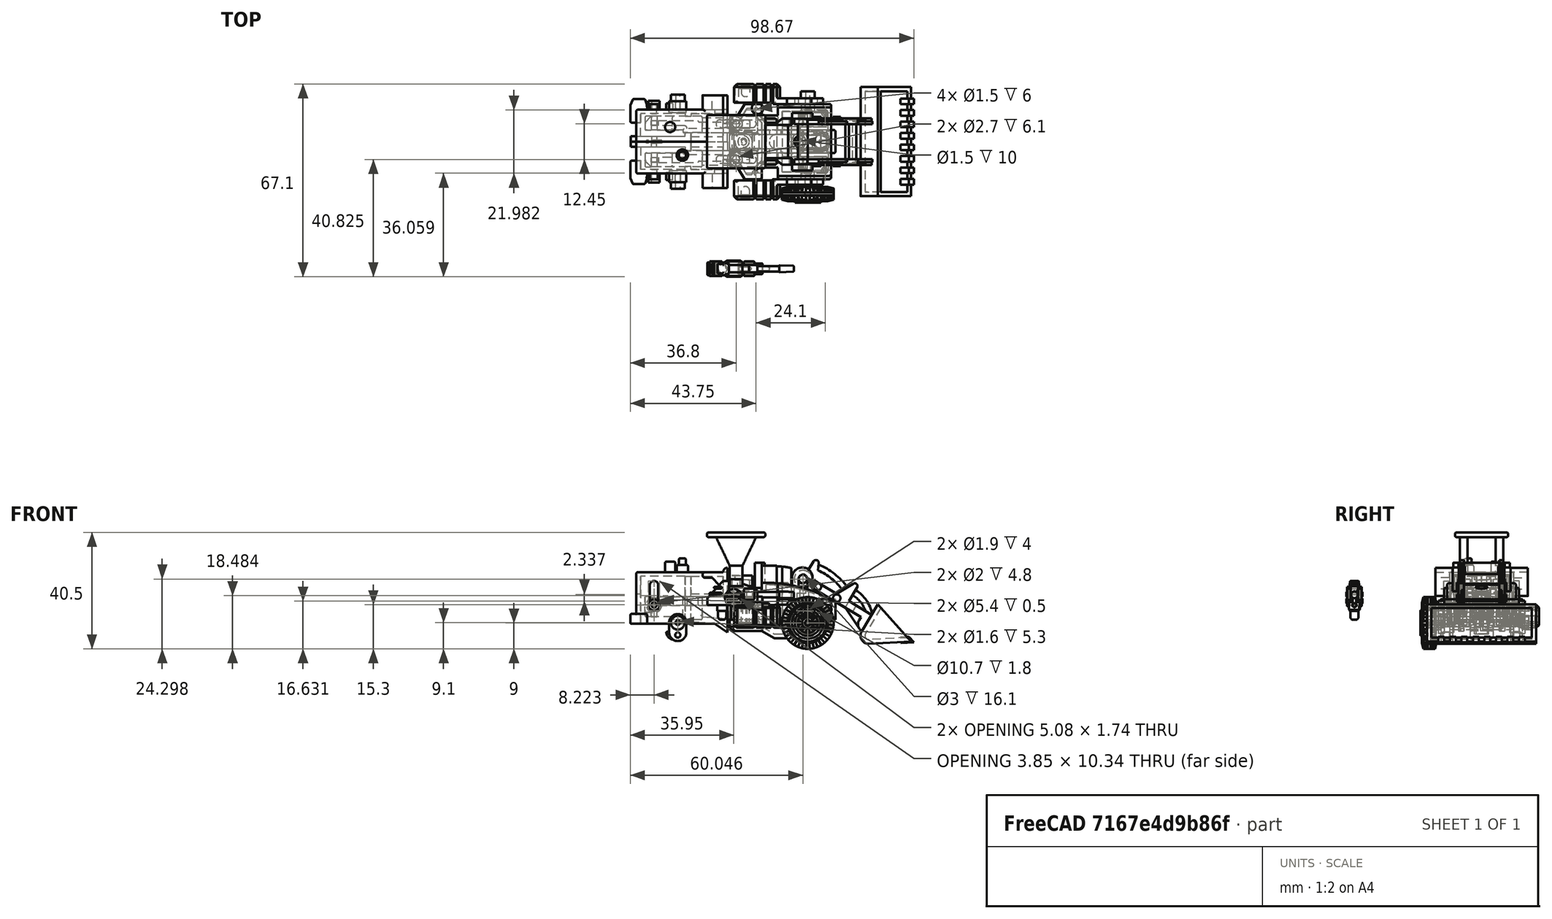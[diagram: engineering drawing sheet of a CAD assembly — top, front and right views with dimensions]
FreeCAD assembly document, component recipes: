
FREECAD ASSEMBLY — COMPONENT RECIPES ("Scrapper")

This assembly document has 14 components, labeled P0..P13 below (a component is one placed body or linked part). 14 of them carry a construction recipe — the FreeCAD feature program that regenerates the part from scratch, quoted from this document or its linked companion documents; the rest are supplied as boundary geometry only. No exploded tour is included for this assembly.
NOTE — this tour is split across 4 documents so each fits a 32k-token context. This is document 1: the component sections continue in the remaining 3 documents, each repeating the header above.
COMPONENT P0 — recipe-attached ("Rear_Torso", modeled in this document).
Construction recipe (the document's own serialized feature program — sketch geometry with constraints, then the solid features built on it; lengths are millimeters unless a unit is written):

FEATURE [Sketcher::SketchObject] Sketch
  ArcFitTolerance = 1e-06
  AttachmentSupport = -> [XY_Plane]
  FullyConstrained = true
  MakeInternals = false
  MapMode = 5
  sketch-geometry (50):
    g0: LineSegment StartX=0 StartY=13.05 StartZ=0 EndX=0 EndY=-13.05 EndZ=0
    g1: LineSegment StartX=0 StartY=-13.05 StartZ=0 EndX=-18.5 EndY=-13.05 EndZ=0
    g2: LineSegment StartX=0 StartY=13.05 StartZ=0 EndX=-18.5 EndY=13.05 EndZ=0
    g3: LineSegment StartX=-17 StartY=10.55 StartZ=0 EndX=-3.5 EndY=10.55 EndZ=0
    g4: LineSegment StartX=-1.5 StartY=5.2 StartZ=0 EndX=-10.8 EndY=5.2 EndZ=0
    g5: LineSegment StartX=-10.8 StartY=5.2 StartZ=0 EndX=-10.8 EndY=3 EndZ=0
    g6: LineSegment StartX=-10.8 StartY=3 StartZ=0 EndX=-1.5 EndY=3 EndZ=0
    g7: LineSegment StartX=-1.5 StartY=3 StartZ=0 EndX=-1.5 EndY=-3 EndZ=0
    g8: LineSegment StartX=-1.5 StartY=-3 StartZ=0 EndX=-10.8 EndY=-3 EndZ=0
    g9: LineSegment StartX=-10.8 StartY=-3 StartZ=0 EndX=-10.8 EndY=-5.2 EndZ=0
    g10: LineSegment StartX=-10.8 StartY=-5.2 StartZ=0 EndX=-1.5 EndY=-5.2 EndZ=0
    g11: LineSegment StartX=-3.5 StartY=-10.55 StartZ=0 EndX=-17 EndY=-10.55 EndZ=0
    g12: ArcOfCircle CenterX=-1.5 CenterY=10.55 CenterZ=0 NormalX=0 NormalY=0 NormalZ=1 AngleXU=0 Radius=2 StartAngle=3.14159 EndAngle=4.71239
    g13: LineSegment StartX=-1.5 StartY=8.55 StartZ=0 EndX=-1.5 EndY=5.2 EndZ=0
    g14: ArcOfCircle CenterX=-1.5 CenterY=-10.55 CenterZ=0 NormalX=0 NormalY=0 NormalZ=1 AngleXU=0 Radius=2 StartAngle=1.5708 EndAngle=3.14159
    g15: LineSegment StartX=-1.5 StartY=-5.2 StartZ=0 EndX=-1.5 EndY=-8.55 EndZ=0
    g16: LineSegment StartX=-18.5 StartY=-13.05 StartZ=0 EndX=-18.5 EndY=-9.05 EndZ=0
    g17: LineSegment StartX=-18.5 StartY=-9.05 StartZ=0 EndX=-24.1 EndY=-9.05 EndZ=0
    g18: LineSegment StartX=-24.1 StartY=-9.05 StartZ=0 EndX=-24.1 EndY=-13.05 EndZ=0
    g19: LineSegment StartX=-24.1 StartY=-13.05 StartZ=0 EndX=-30.1 EndY=-13.05 EndZ=0
    g20: LineSegment StartX=-30.1 StartY=-13.05 StartZ=0 EndX=-32.6 EndY=-8.9 EndZ=0
    g21: LineSegment StartX=-32.6 StartY=-8.9 StartZ=0 EndX=-35.3 EndY=-8.9 EndZ=0
    g22: LineSegment StartX=-35.3 StartY=-8.9 StartZ=0 EndX=-35.3 EndY=8.9 EndZ=0
    g23: LineSegment StartX=-35.3 StartY=8.9 StartZ=0 EndX=-32.6 EndY=8.9 EndZ=0
    g24: LineSegment StartX=-32.6 StartY=8.9 StartZ=0 EndX=-30.1 EndY=13.05 EndZ=0
    g25: LineSegment StartX=-30.1 StartY=13.05 StartZ=0 EndX=-24.1 EndY=13.05 EndZ=0
    g26: LineSegment StartX=-24.1 StartY=13.05 StartZ=0 EndX=-24.1 EndY=9.05 EndZ=0
    g27: LineSegment StartX=-24.1 StartY=9.05 StartZ=0 EndX=-18.5 EndY=9.05 EndZ=0
    g28: LineSegment StartX=-18.5 StartY=9.05 StartZ=0 EndX=-18.5 EndY=13.05 EndZ=0
    g29: LineSegment StartX=-17 StartY=-10.55 StartZ=0 EndX=-17 EndY=-8.55 EndZ=0
    g30: ArcOfCircle CenterX=-18 CenterY=-8.55 CenterZ=0 NormalX=0 NormalY=0 NormalZ=1 AngleXU=0 Radius=1 StartAngle=5e-16 EndAngle=1.5708
    g31: LineSegment StartX=-18 StartY=-7.55 StartZ=0 EndX=-24.6 EndY=-7.55 EndZ=0
    g32: ArcOfCircle CenterX=-24.6 CenterY=-8.55 CenterZ=0 NormalX=0 NormalY=0 NormalZ=1 AngleXU=0 Radius=1 StartAngle=1.5708 EndAngle=3.14159
    g33: LineSegment StartX=-25.6 StartY=-8.55 StartZ=0 EndX=-25.6 EndY=-9.55 EndZ=0
    g34: ArcOfCircle CenterX=-25.6 CenterY=-11.55 CenterZ=0 NormalX=0 NormalY=0 NormalZ=1 AngleXU=0 Radius=2 StartAngle=1.5708 EndAngle=3.14159
    g35: LineSegment StartX=-27.6 StartY=-11.55 StartZ=0 EndX=-29.27 EndY=-11.55 EndZ=0
    g36: LineSegment StartX=-29.27 StartY=-11.55 StartZ=0 EndX=-31.4373 EndY=-7.95236 EndZ=0
    g37: ArcOfCircle CenterX=-32.6 CenterY=-8.9 CenterZ=0 NormalX=0 NormalY=0 NormalZ=1 AngleXU=0 Radius=1.5 StartAngle=0.683822 EndAngle=1.5708
    g38: LineSegment StartX=-32.6 StartY=-7.4 StartZ=0 EndX=-33.8 EndY=-7.4 EndZ=0
    g39: LineSegment StartX=-33.8 StartY=-7.4 StartZ=0 EndX=-33.8 EndY=7.4 EndZ=0
    g40: LineSegment StartX=-33.8 StartY=7.4 StartZ=0 EndX=-32.6 EndY=7.4 EndZ=0
    g41: ArcOfCircle CenterX=-32.6 CenterY=8.9 CenterZ=0 NormalX=0 NormalY=0 NormalZ=1 AngleXU=0 Radius=1.5 StartAngle=4.71239 EndAngle=5.59936
    g42: LineSegment StartX=-31.4373 StartY=7.95236 StartZ=0 EndX=-29.27 EndY=11.55 EndZ=0
    g43: LineSegment StartX=-29.27 StartY=11.55 StartZ=0 EndX=-27.6 EndY=11.55 EndZ=0
    g44: ArcOfCircle CenterX=-25.6 CenterY=11.55 CenterZ=0 NormalX=0 NormalY=0 NormalZ=1 AngleXU=0 Radius=2 StartAngle=3.14159 EndAngle=4.71239
    g45: LineSegment StartX=-25.6 StartY=9.55 StartZ=0 EndX=-25.6 EndY=8.55 EndZ=0
    g46: ArcOfCircle CenterX=-24.6 CenterY=8.55 CenterZ=0 NormalX=0 NormalY=0 NormalZ=1 AngleXU=0 Radius=1 StartAngle=3.14159 EndAngle=4.71239
    g47: LineSegment StartX=-24.6 StartY=7.55 StartZ=0 EndX=-18 EndY=7.55 EndZ=0
    g48: ArcOfCircle CenterX=-18 CenterY=8.55 CenterZ=0 NormalX=0 NormalY=0 NormalZ=1 AngleXU=0 Radius=1 StartAngle=4.71239 EndAngle=6.28319
    g49: LineSegment StartX=-17 StartY=8.55 StartZ=0 EndX=-17 EndY=10.55 EndZ=0
  constraints (158):
    c: Vertical(g0)
    c: Coincident(g1,g0)
    c: Horizontal(g1)
    c: Coincident(g2,g0)
    c: Horizontal(g2)
    c: DistanceY(g0,g0) = 26.1
    c: DistanceY(g-1,g0) = 13.05
    c: PointOnObject(g-1,g0)
    c: DistanceX(g2,g2) = 18.5
    c: DistanceX(g1,g1) = 18.5
    c: Horizontal(g3)
    c: Horizontal(g4)
    c: Coincident(g5,g4)
    c: Vertical(g5)
    c: Coincident(g6,g5)
    c: Horizontal(g6)
    c: Coincident(g7,g6)
    c: Vertical(g7)
    c: Coincident(g8,g7)
    c: Horizontal(g8)
    c: Coincident(g9,g8)
    c: Vertical(g9)
    c: Coincident(g10,g9)
    c: Horizontal(g10)
    c: Horizontal(g11)
    c: DistanceY(g5,g5) = 2.2
    c: DistanceY(g9,g9) = 2.2
    c: DistanceY(g3,g0) = 2.5
    c: DistanceY(g0,g11) = 2.5
    c: Coincident(g12,g3)
    c: Coincident(g13,g12)
    c: Coincident(g13,g4)
    c: Vertical(g13)
    c: Coincident(g14,g11)
    c: Coincident(g15,g10)
    c: Coincident(g15,g14)
    c: Vertical(g15)
    c: DistanceX(g14,g0) = 1.5
    c: DistanceX(g7,g-1) = 1.5
    c: DistanceX(g12,g0) = 1.5
    c: DistanceY(g12,g3) = 0
    c: DistanceY(g11,g14) = 0
    c: DistanceX(g14,g14) = 0
    c: Radius(g12) = 2
    c: Radius(g14) = 2
    c: DistanceY(g7,g7) = 6
    c: DistanceY(g7,g-1) = 3
    c: DistanceX(g12,g12) = 0
    c: DistanceX(g6,g6) = 9.3
    c: DistanceX(g8,g8) = 9.3
    c: Coincident(g16,g1)
    c: Vertical(g16)
    c: Coincident(g17,g16)
    c: Horizontal(g17)
    c: Coincident(g18,g17)
    c: Vertical(g18)
    c: Coincident(g19,g18)
    c: Horizontal(g19)
    c: Coincident(g20,g19)
    c: Coincident(g21,g20)
    c: Horizontal(g21)
    c: Coincident(g22,g21)
    c: Vertical(g22)
    c: Coincident(g23,g22)
    c: Horizontal(g23)
    c: Coincident(g24,g23)
    c: Coincident(g25,g24)
    c: Horizontal(g25)
    c: Coincident(g26,g25)
    c: Vertical(g26)
    c: Coincident(g27,g26)
    c: Horizontal(g27)
    c: Coincident(g28,g27)
    c: Coincident(g28,g2)
    c: Vertical(g28)
    c: DistanceX(g27,g27) = 5.6
    c: DistanceX(g17,g17) = 5.6
    c: DistanceY(g16,g16) = 4
    c: DistanceY(g18,g18) = 4
    c: DistanceY(g28,g28) = 4
    c: DistanceY(g26,g26) = 4
    c: DistanceX(g25,g25) = 6
    c: DistanceX(g19,g19) = 6
    c: DistanceX(g22,g-1) = 35.3
    c: DistanceX(g23,g23) = 2.7
    c: DistanceX(g21,g21) = 2.7
    c: DistanceY(g22,g22) = 17.8
    c: DistanceY(g-1,g22) = 8.9
    c: Coincident(g29,g11)
    c: Vertical(g29)
    c: Coincident(g30,g29)
    c: Coincident(g31,g30)
    c: Horizontal(g31)
    c: Coincident(g32,g31)
    c: Coincident(g33,g32)
    c: Vertical(g33)
    c: Coincident(g34,g33)
    c: Coincident(g35,g34)
    c: Horizontal(g35)
    c: Coincident(g36,g35)
    c: Coincident(g37,g36)
    c: Coincident(g38,g37)
    c: Horizontal(g38)
    c: Coincident(g39,g38)
    c: Vertical(g39)
    c: Coincident(g40,g39)
    c: Horizontal(g40)
    c: Coincident(g41,g40)
    c: Coincident(g42,g41)
    c: Coincident(g43,g42)
    c: Horizontal(g43)
    c: Coincident(g44,g43)
    c: Coincident(g45,g44)
    c: Vertical(g45)
    c: Coincident(g46,g45)
    c: Coincident(g47,g46)
    c: Horizontal(g47)
    c: Coincident(g48,g47)
    c: Coincident(g49,g48)
    c: Coincident(g49,g3)
    c: Vertical(g49)
    c: DistanceX(g22,g39) = 1.5
    c: DistanceY(g46,g26) = 1.5
    c: DistanceY(g17,g31) = 1.5
    c: DistanceX(g16,g29) = 1.5
    c: DistanceX(g32,g17) = 1.5
    c: DistanceX(g45,g26) = 1.5
    c: DistanceX(g27,g48) = 1.5
    c: DistanceY(g48,g48) = 0
    c: DistanceY(g29,g30) = 0
    c: DistanceX(g30,g30) = 0
    c: DistanceX(g32,g31) = 0
    c: DistanceX(g48,g47) = 0
    c: DistanceX(g46,g46) = 0
    c: DistanceY(g46,g45) = 0
    c: Radius(g48) = 1
    c: Radius(g46) = 1
    c: Radius(g30) = 1
    c: Radius(g32) = 1
    c: DistanceY(g32,g32) = 0
    c: Parallel(g20,g36)
    c: Parallel(g42,g24)
    c: DistanceX(g40,g41) = 0
    c: DistanceX(g37,g37) = 0
    c: DistanceY(g20,g38) = 1.5
    c: DistanceY(g39,g23) = 1.5
    c: DistanceX(g34,g33) = 0
    c: DistanceX(g44,g44) = 0
    c: DistanceY(g43,g44) = 0
    c: DistanceY(g34,g34) = 0
    c: Radius(g34) = 2
    c: Radius(g44) = 2
    c: DistanceY(g19,g35) = 1.5
    c: DistanceY(g42,g24) = 1.5
    c: Coincident(g41,g23)
    c: Coincident(g37,g20)
    c: Distance(g36) = 4.2
    c: Distance(g42) = 4.2
FEATURE [PartDesign::Pad] Pad
  Direction = (0,0,1)
  Length = 2
  Length2 = 10
  Profile = -> Sketch
  ReferenceAxis = -> Sketch [N_Axis]
  Refine = true
  Suppressed = false
  Type = 0
FEATURE [Sketcher::SketchObject] Sketch001
  ArcFitTolerance = 1e-06
  AttachmentSupport = -> [Pad]
  ExternalGeometry = -> [Pad]
  FullyConstrained = true
  MakeInternals = false
  MapMode = 5
  Placement = pos=(0,-13.05,0) rot=(1,0,0;1.5708rad)
  sketch-geometry (3):
    g0: LineSegment StartX=-18.5 StartY=2 StartZ=0 EndX=-18.5 EndY=7.6 EndZ=0
    g1: ArcOfCircle CenterX=-22.8718 CenterY=-40.2005 CenterZ=0 NormalX=0 NormalY=0 NormalZ=1 AngleXU=0 Radius=48 StartAngle=1.07413 EndAngle=1.47959
    g2: LineSegment StartX=-18.5 StartY=2 StartZ=0 EndX=0 EndY=2 EndZ=0
  constraints (8):
    c: Coincident(g0,g-3)
    c: Vertical(g0)
    c: Coincident(g1,g0)
    c: Coincident(g1,g-3)
    c: Coincident(g2,g0)
    c: Coincident(g2,g-3)
    c: DistanceY(g0,g0) = 5.6
    c: Radius(g1) = 48
FEATURE [PartDesign::Pad] Pad001
  BaseFeature = -> Pad
  Direction = (0,-1,2e-16)
  Length = 25
  Length2 = 10
  Profile = -> Sketch001
  ReferenceAxis = -> Sketch001 [N_Axis]
  Refine = true
  Reversed = true
  Suppressed = false
  Type = 0
FEATURE [Sketcher::SketchObject] Sketch002
  ArcFitTolerance = 1e-06
  AttachmentSupport = -> [Pad001]
  ExternalGeometry = -> [Pad001]
  FullyConstrained = true
  MakeInternals = false
  MapMode = 5
  Placement = pos=(0,-13.05,3.7e-15) rot=(1,0,0;1.5708rad)
  sketch-geometry (3):
    g0: LineSegment StartX=-17 StartY=2 StartZ=0 EndX=-1.5 EndY=2 EndZ=0
    g1: LineSegment StartX=-17 StartY=2 StartZ=0 EndX=-17 EndY=6.7373 EndZ=0
    g2: ArcOfCircle CenterX=-22.8718 CenterY=-40.2005 CenterZ=0 NormalX=0 NormalY=0 NormalZ=1 AngleXU=0 Radius=47.3036 StartAngle=1.10201 EndAngle=1.44635
  constraints (9):
    c: Horizontal(g0)
    c: Coincident(g1,g0)
    c: Vertical(g1)
    c: Coincident(g2,g1)
    c: Coincident(g2,g0)
    c: Coincident(g2,g-3)
    c: DistanceY(g-4,g0) = 2
    c: DistanceX(g-4,g0) = 1.5
    c: DistanceX(g0,g-5) = 1.5
FEATURE [PartDesign::Pocket] Pocket
  BaseFeature = -> Pad001
  Direction = (0,1,-2e-16)
  Length = 23.6
  Length2 = 5
  Profile = -> Sketch002
  ReferenceAxis = -> Sketch002 [N_Axis]
  Refine = true
  Suppressed = false
  Type = 0
FEATURE [Sketcher::SketchObject] Sketch003
  ArcFitTolerance = 1e-06
  AttachmentSupport = -> [Pocket]
  ExternalGeometry = -> [Pocket]
  FullyConstrained = true
  MakeInternals = false
  MapMode = 5
  Placement = pos=(0,-13.05,3.7e-15) rot=(1,0,0;1.5708rad)
  sketch-geometry (3):
    g0: LineSegment StartX=0 StartY=2 StartZ=0 EndX=-18.5 EndY=2 EndZ=0
    g1: LineSegment StartX=-18.5 StartY=2 StartZ=0 EndX=-18.5 EndY=7.6 EndZ=0
    g2: ArcOfCircle CenterX=-22.8718 CenterY=-40.2005 CenterZ=0 NormalX=0 NormalY=0 NormalZ=1 AngleXU=0 Radius=48 StartAngle=1.07413 EndAngle=1.47959
  constraints (8):
    c: Coincident(g0,g-4)
    c: PointOnObject(g0,g-5)
    c: Horizontal(g0)
    c: Coincident(g1,g0)
    c: Coincident(g1,g-5)
    c: Coincident(g2,g1)
    c: Coincident(g2,g0)
    c: Tangent(g2,g-4)
FEATURE [PartDesign::Pocket] Pocket001
  BaseFeature = -> Pocket
  Direction = (0,1,-2e-16)
  Length = 1.1
  Length2 = 5
  Profile = -> Sketch003
  ReferenceAxis = -> Sketch003 [N_Axis]
  Refine = true
  Suppressed = false
  Type = 0
FEATURE [Sketcher::SketchObject] Sketch004
  ArcFitTolerance = 1e-06
  AttachmentSupport = -> [Pocket001]
  ExternalGeometry = -> [Pocket001]
  FullyConstrained = true
  MakeInternals = false
  MapMode = 5
  Placement = pos=(0,-11.95,4.5e-15) rot=(1,0,0;1.5708rad)
  sketch-geometry (3):
    g0: LineSegment StartX=-17 StartY=6.7373 StartZ=0 EndX=-17 EndY=2 EndZ=0
    g1: LineSegment StartX=-17 StartY=2 StartZ=0 EndX=-1.5 EndY=2 EndZ=0
    g2: ArcOfCircle CenterX=-22.8718 CenterY=-40.2005 CenterZ=0 NormalX=0 NormalY=0 NormalZ=1 AngleXU=0 Radius=47.3036 StartAngle=1.10201 EndAngle=1.44635
  constraints (7):
    c: Coincident(g0,g-4)
    c: Coincident(g0,g-4)
    c: Coincident(g1,g0)
    c: Coincident(g1,g-3)
    c: Coincident(g2,g0)
    c: Coincident(g2,g1)
    c: Tangent(g2,g-3)
FEATURE [PartDesign::Pad] Pad002
  BaseFeature = -> Pocket001
  Direction = (0,-1,2e-16)
  Length = 1.4
  Length2 = 10
  Profile = -> Sketch004
  ReferenceAxis = -> Sketch004 [N_Axis]
  Refine = true
  Reversed = true
  Suppressed = false
  Type = 0
FEATURE [Sketcher::SketchObject] Sketch005
  ArcFitTolerance = 1e-06
  AttachmentSupport = -> [Pad002]
  ExternalGeometry = -> [Pad002]
  FullyConstrained = true
  MakeInternals = false
  MapMode = 5
  Placement = pos=(0,-9.05,0) rot=(1,0,0;1.5708rad)
  sketch-geometry (4):
    g0: LineSegment StartX=-18.5 StartY=7.6 StartZ=0 EndX=-18.5 EndY=2 EndZ=0
    g1: LineSegment StartX=-18.5 StartY=2 StartZ=0 EndX=-24.1 EndY=2 EndZ=0
    g2: LineSegment StartX=-24.1 StartY=2 StartZ=0 EndX=-24.1 EndY=7.78379 EndZ=0
    g3: ArcOfCircle CenterX=-22.8718 CenterY=-40.2005 CenterZ=0 NormalX=0 NormalY=0 NormalZ=1 AngleXU=0 Radius=48 StartAngle=1.47959 EndAngle=1.59639
  constraints (9):
    c: Coincident(g0,g-4)
    c: Coincident(g0,g-4)
    c: Coincident(g1,g0)
    c: Coincident(g1,g-3)
    c: Coincident(g2,g1)
    c: Vertical(g2)
    c: Coincident(g3,g0)
    c: Coincident(g3,g2)
    c: Coincident(g3,g-5)
FEATURE [PartDesign::Pad] Pad003
  BaseFeature = -> Pad002
  Direction = (0,-1,2e-16)
  Length = 18.1
  Length2 = 10
  Profile = -> Sketch005
  ReferenceAxis = -> Sketch005 [N_Axis]
  Refine = true
  Reversed = true
  Suppressed = false
  Type = 0
FEATURE [Sketcher::SketchObject] Sketch006
  ArcFitTolerance = 1e-06
  AttachmentSupport = -> [Pad003]
  ExternalGeometry = -> [Pad003]
  FullyConstrained = true
  MakeInternals = false
  MapMode = 5
  Placement = pos=(0,11.95,-4.5e-15) rot=(0,0.707107,0.707107;3.14159rad)
  sketch-geometry (4):
    g0: LineSegment StartX=24.1 StartY=2 StartZ=0 EndX=17 EndY=2 EndZ=0
    g1: LineSegment StartX=17 StartY=2 StartZ=0 EndX=17 EndY=6.73 EndZ=0
    g2: LineSegment StartX=24.1 StartY=2 StartZ=0 EndX=24.1 EndY=7.07995 EndZ=0
    g3: ArcOfCircle CenterX=22.8718 CenterY=-40.2005 CenterZ=0 NormalX=0 NormalY=0 NormalZ=1 AngleXU=0 Radius=47.2964 StartAngle=1.54482 EndAngle=1.69527
  constraints (11):
    c: Coincident(g0,g-5)
    c: PointOnObject(g0,g-4)
    c: Coincident(g1,g0)
    c: Vertical(g1)
    c: Coincident(g2,g0)
    c: PointOnObject(g2,g-5)
    c: Coincident(g3,g1)
    c: Coincident(g3,g2)
    c: Coincident(g3,g-3)
    c: DistanceX(g0,g-4) = 1.5
    c: DistanceY(g1,g1) = 4.73
FEATURE [PartDesign::Pocket] Pocket002
  BaseFeature = -> Pad003
  Direction = (0,-1,2e-16)
  Length = 24
  Length2 = 5
  Profile = -> Sketch006
  ReferenceAxis = -> Sketch006 [N_Axis]
  Refine = true
  Suppressed = false
  Type = 0
FEATURE [Sketcher::SketchObject] Sketch007
  ArcFitTolerance = 1e-06
  AttachmentSupport = -> [Pocket002]
  ExternalGeometry = -> [Pocket002]
  FullyConstrained = true
  MakeInternals = false
  MapMode = 5
  Placement = pos=(0,0,2) rot=(0,0,1;0rad)
  sketch-geometry (5):
    g0: LineSegment StartX=-17 StartY=-11.95 StartZ=0 EndX=-18.5 EndY=-11.95 EndZ=0
    g1: LineSegment StartX=-18.5 StartY=-11.95 StartZ=0 EndX=-18.5 EndY=-7.55 EndZ=0
    g2: LineSegment StartX=-17 StartY=-11.95 StartZ=0 EndX=-17 EndY=-8.55 EndZ=0
    g3: LineSegment StartX=-18.5 StartY=-7.55 StartZ=0 EndX=-18 EndY=-7.55 EndZ=0
    g4: ArcOfCircle CenterX=-18 CenterY=-8.55001 CenterZ=0 NormalX=0 NormalY=0 NormalZ=1 AngleXU=0 Radius=1.00001 StartAngle=6.04686e-06 EndAngle=1.57079
  constraints (13):
    c: Coincident(g0,g-6)
    c: PointOnObject(g0,g-5)
    c: Horizontal(g0)
    c: Coincident(g1,g0)
    c: Vertical(g1)
    c: Coincident(g2,g0)
    c: Coincident(g2,g-4)
    c: PointOnObject(g1,g-7)
    c: Coincident(g3,g1)
    c: Coincident(g3,g-7)
    c: Coincident(g4,g3)
    c: Coincident(g4,g2)
    c: Tangent(g4,g-4)
FEATURE [PartDesign::Pad] Pad004
  BaseFeature = -> Pocket002
  Direction = (0,0,1)
  Length = 5
  Length2 = 10
  Profile = -> Sketch007
  ReferenceAxis = -> Sketch007 [N_Axis]
  Refine = true
  Suppressed = false
  Type = 0
FEATURE [Sketcher::SketchObject] Sketch008
  ArcFitTolerance = 1e-06
  AttachmentSupport = -> [Pad004]
  ExternalGeometry = -> [Pad004]
  FullyConstrained = true
  MakeInternals = false
  MapMode = 5
  Placement = pos=(0,0,2) rot=(0,0,1;0rad)
  sketch-geometry (4):
    g0: LineSegment StartX=-18.5 StartY=-7.55 StartZ=0 EndX=-24.1 EndY=-7.55 EndZ=0
    g1: LineSegment StartX=-24.1 StartY=-7.55 StartZ=0 EndX=-24.1 EndY=-9.05 EndZ=0
    g2: LineSegment StartX=-24.1 StartY=-9.05 StartZ=0 EndX=-18.5 EndY=-9.05 EndZ=0
    g3: LineSegment StartX=-18.5 StartY=-9.05 StartZ=0 EndX=-18.5 EndY=-7.55 EndZ=0
  constraints (10):
    c: Coincident(g0,g1)
    c: Coincident(g1,g2)
    c: Coincident(g2,g3)
    c: Coincident(g3,g0)
    c: Horizontal(g0)
    c: Horizontal(g2)
    c: Vertical(g1)
    c: Vertical(g3)
    c: Coincident(g0,g-4)
    c: Coincident(g1,g-5)
FEATURE [PartDesign::Pad] Pad005
  BaseFeature = -> Pad004
  Direction = (0,0,1)
  Length = 5.1
  Length2 = 10
  Profile = -> Sketch008
  ReferenceAxis = -> Sketch008 [N_Axis]
  Refine = true
  Suppressed = false
  Type = 0
FEATURE [Sketcher::SketchObject] Sketch009
  ArcFitTolerance = 1e-06
  AttachmentSupport = -> [Pad005]
  ExternalGeometry = -> [Pad005]
  FullyConstrained = true
  MakeInternals = false
  MapMode = 5
  Placement = pos=(0,0,2) rot=(0,0,1;0rad)
  sketch-geometry (5):
    g0: LineSegment StartX=-17 StartY=11.95 StartZ=0 EndX=-18.5 EndY=11.95 EndZ=0
    g1: LineSegment StartX=-18.5 StartY=11.95 StartZ=0 EndX=-18.5 EndY=7.55 EndZ=0
    g2: LineSegment StartX=-17 StartY=11.95 StartZ=0 EndX=-17 EndY=8.55 EndZ=0
    g3: LineSegment StartX=-18.5 StartY=7.55 StartZ=0 EndX=-18 EndY=7.55 EndZ=0
    g4: ArcOfCircle CenterX=-18 CenterY=8.55001 CenterZ=0 NormalX=0 NormalY=0 NormalZ=1 AngleXU=0 Radius=1.00001 StartAngle=4.7124 EndAngle=6.28318
  constraints (13):
    c: Coincident(g0,g-7)
    c: PointOnObject(g0,g-3)
    c: Horizontal(g0)
    c: Coincident(g1,g0)
    c: PointOnObject(g1,g-4)
    c: Vertical(g1)
    c: Coincident(g2,g0)
    c: Coincident(g2,g-6)
    c: Coincident(g3,g1)
    c: Coincident(g3,g-5)
    c: Coincident(g4,g3)
    c: Tangent(g4,g-5)
    c: Coincident(g4,g2)
FEATURE [PartDesign::Pad] Pad006
  BaseFeature = -> Pad005
  Direction = (0,0,1)
  Length = 5
  Length2 = 10
  Profile = -> Sketch009
  ReferenceAxis = -> Sketch009 [N_Axis]
  Refine = true
  Suppressed = false
  Type = 0
FEATURE [Sketcher::SketchObject] Sketch010
  ArcFitTolerance = 1e-06
  AttachmentSupport = -> [Pad006]
  ExternalGeometry = -> [Pad006]
  FullyConstrained = true
  MakeInternals = false
  MapMode = 5
  Placement = pos=(0,0,2) rot=(0,0,1;0rad)
  sketch-geometry (4):
    g0: LineSegment StartX=-18.5 StartY=7.55 StartZ=0 EndX=-18.5 EndY=9.05 EndZ=0
    g1: LineSegment StartX=-18.5 StartY=9.05 StartZ=0 EndX=-24.1 EndY=9.05 EndZ=0
    g2: LineSegment StartX=-24.1 StartY=9.05 StartZ=0 EndX=-24.1 EndY=7.55 EndZ=0
    g3: LineSegment StartX=-24.1 StartY=7.55 StartZ=0 EndX=-18.5 EndY=7.55 EndZ=0
  constraints (10):
    c: Coincident(g0,g1)
    c: Coincident(g1,g2)
    c: Coincident(g2,g3)
    c: Coincident(g3,g0)
    c: Vertical(g0)
    c: Vertical(g2)
    c: Horizontal(g1)
    c: Horizontal(g3)
    c: Coincident(g0,g-5)
    c: Coincident(g1,g-4)
FEATURE [PartDesign::Pad] Pad007
  BaseFeature = -> Pad006
  Direction = (0,0,1)
  Length = 5.1
  Length2 = 10
  Profile = -> Sketch010
  ReferenceAxis = -> Sketch010 [N_Axis]
  Refine = true
  Suppressed = false
  Type = 0
FEATURE [PartDesign::Pad] Pad008
  BaseFeature = -> Pad007
  Direction = (0,0,1)
  Length = 4
  Length2 = 10
  Profile = -> Pad007 [Face55]
  Refine = true
  Suppressed = false
  Type = 0
FEATURE [Sketcher::SketchObject] Sketch011
  ArcFitTolerance = 1e-06
  AttachmentSupport = -> [Pad008]
  ExternalGeometry = -> [Pad008]
  FullyConstrained = true
  MakeInternals = false
  MapMode = 5
  Placement = pos=(0,0,6) rot=(0,0,1;0rad)
  sketch-geometry (18):
    g0: LineSegment StartX=-24.1 StartY=7.55 StartZ=0 EndX=-24.1 EndY=-7.55 EndZ=0
    g1: ArcOfCircle CenterX=-24.6 CenterY=-8.55 CenterZ=0 NormalX=0 NormalY=0 NormalZ=1 AngleXU=0 Radius=1 StartAngle=1.5708 EndAngle=3.14159
    g2: LineSegment StartX=-25.6 StartY=-8.55 StartZ=0 EndX=-25.6 EndY=-9.55 EndZ=0
    g3: ArcOfCircle CenterX=-25.6 CenterY=-11.55 CenterZ=0 NormalX=0 NormalY=0 NormalZ=1 AngleXU=0 Radius=2 StartAngle=1.5708 EndAngle=3.14159
    g4: LineSegment StartX=-27.6 StartY=-11.55 StartZ=0 EndX=-29.27 EndY=-11.55 EndZ=0
    g5: LineSegment StartX=-29.27 StartY=-11.55 StartZ=0 EndX=-31.4373 EndY=-7.95236 EndZ=0
    g6: ArcOfCircle CenterX=-32.6 CenterY=-8.9 CenterZ=0 NormalX=0 NormalY=0 NormalZ=1 AngleXU=0 Radius=1.5 StartAngle=0.683822 EndAngle=1.5708
    g7: LineSegment StartX=-32.6 StartY=-7.4 StartZ=0 EndX=-33.8 EndY=-7.4 EndZ=0
    g8: LineSegment StartX=-33.8 StartY=-7.4 StartZ=0 EndX=-33.8 EndY=7.4 EndZ=0
    g9: LineSegment StartX=-33.8 StartY=7.4 StartZ=0 EndX=-32.6 EndY=7.4 EndZ=0
    g10: ArcOfCircle CenterX=-25.6 CenterY=11.55 CenterZ=0 NormalX=0 NormalY=0 NormalZ=1 AngleXU=0 Radius=1.99999 StartAngle=3.14159 EndAngle=4.71239
    g11: LineSegment StartX=-27.6 StartY=11.55 StartZ=0 EndX=-29.27 EndY=11.55 EndZ=0
    g12: LineSegment StartX=-29.27 StartY=11.55 StartZ=0 EndX=-31.4373 EndY=7.95236 EndZ=0
    g13: ArcOfCircle CenterX=-32.6 CenterY=8.90002 CenterZ=0 NormalX=0 NormalY=0 NormalZ=1 AngleXU=0 Radius=1.50002 StartAngle=4.71239 EndAngle=5.59936
    g14: LineSegment StartX=-24.6 StartY=-7.55 StartZ=0 EndX=-24.1 EndY=-7.55 EndZ=0
    g15: LineSegment StartX=-24.1 StartY=7.55 StartZ=0 EndX=-24.6 EndY=7.55 EndZ=0
    g16: ArcOfCircle CenterX=-24.6 CenterY=8.55 CenterZ=0 NormalX=0 NormalY=0 NormalZ=1 AngleXU=0 Radius=1 StartAngle=3.14159 EndAngle=4.71239
    g17: LineSegment StartX=-25.6 StartY=9.55 StartZ=0 EndX=-25.6 EndY=8.55 EndZ=0
  constraints (38):
    c: Coincident(g0,g-16)
    c: Tangent(g1,g-15) = -1.5708
    c: Coincident(g3,g2)
    c: Tangent(g3,g-13) = -1.5708
    c: Coincident(g2,g-14)
    c: Coincident(g2,g1)
    c: Coincident(g4,g3)
    c: Coincident(g4,g-12)
    c: Coincident(g5,g4)
    c: Coincident(g5,g-11)
    c: Coincident(g6,g5)
    c: Tangent(g6,g-10) = -1.5708
    c: Coincident(g7,g-9)
    c: Coincident(g7,g6)
    c: Coincident(g8,g7)
    c: Coincident(g8,g-8)
    c: Coincident(g9,g8)
    c: Coincident(g9,g-7)
    c: Coincident(g10,g-4)
    c: Coincident(g11,g10)
    c: Coincident(g11,g-5)
    c: Coincident(g12,g11)
    c: Coincident(g12,g-6)
    c: Coincident(g13,g12)
    c: Coincident(g13,g9)
    c: Tangent(g13,g-6)
    c: Tangent(g10,g-3)
    c: Coincident(g1,g-16)
    c: Coincident(g14,g1)
    c: Coincident(g14,g0)
    c: Coincident(g15,g-19)
    c: Coincident(g15,g0)
    c: Coincident(g0,g-19)
    c: Coincident(g10,g-17)
    c: Coincident(g16,g15)
    c: Tangent(g16,g-18) = -1.5708
    c: Coincident(g17,g10)
    c: Coincident(g17,g-18)
FEATURE [PartDesign::Pad] Pad009
  BaseFeature = -> Pad008
  Direction = (0,0,1)
  Length = 1.5
  Length2 = 10
  Profile = -> Sketch011
  ReferenceAxis = -> Sketch011 [N_Axis]
  Refine = true
  Reversed = true
  Suppressed = false
  Type = 0
FEATURE [Sketcher::SketchObject] Sketch012
  ArcFitTolerance = 1e-06
  AttachmentSupport = -> [Pad009]
  ExternalGeometry = -> [Pad009]
  FullyConstrained = true
  MakeInternals = false
  MapMode = 5
  Placement = pos=(0,0,4.5) rot=(1,0,0;3.14159rad)
  sketch-geometry (4):
    g0: LineSegment StartX=-24.1 StartY=7.55 StartZ=0 EndX=-24.1 EndY=-7.55 EndZ=0
    g1: LineSegment StartX=-24.1 StartY=-7.55 StartZ=0 EndX=-22.6 EndY=-7.55 EndZ=0
    g2: LineSegment StartX=-22.6 StartY=-7.55 StartZ=0 EndX=-22.6 EndY=7.55 EndZ=0
    g3: LineSegment StartX=-22.6 StartY=7.55 StartZ=0 EndX=-24.1 EndY=7.55 EndZ=0
  constraints (11):
    c: Coincident(g0,g1)
    c: Coincident(g1,g2)
    c: Coincident(g2,g3)
    c: Coincident(g3,g0)
    c: Vertical(g0)
    c: Vertical(g2)
    c: Horizontal(g1)
    c: Horizontal(g3)
    c: Coincident(g0,g-3)
    c: PointOnObject(g1,g-5)
    c: DistanceX(g1,g1) = 1.5
FEATURE [PartDesign::Pad] Pad010
  BaseFeature = -> Pad009
  Direction = (0,0,-1)
  Length = 3
  Length2 = 10
  Profile = -> Sketch012
  ReferenceAxis = -> Sketch012 [N_Axis]
  Refine = true
  Reversed = true
  Suppressed = false
  Type = 0
FEATURE [Sketcher::SketchObject] Sketch013
  ArcFitTolerance = 1e-06
  AttachmentSupport = -> [Pad010]
  ExternalGeometry = -> [Pad010]
  FullyConstrained = true
  MakeInternals = false
  MapMode = 5
  Placement = pos=(0,5.2,0) rot=(0,0.707107,0.707107;3.14159rad)
  sketch-geometry (3):
    g0: LineSegment StartX=1.5 StartY=2 StartZ=0 EndX=10.8 EndY=2 EndZ=0
    g1: LineSegment StartX=10.8 StartY=2 StartZ=0 EndX=10.8 EndY=5.53687 EndZ=0
    g2: ArcOfCircle CenterX=22.8718 CenterY=-40.2005 CenterZ=0 NormalX=0 NormalY=0 NormalZ=1 AngleXU=0 Radius=47.3036 StartAngle=1.82885 EndAngle=2.03958
  constraints (8):
    c: Coincident(g0,g-4)
    c: Coincident(g0,g-3)
    c: Coincident(g1,g0)
    c: PointOnObject(g1,g-4)
    c: Vertical(g1)
    c: Coincident(g2,g0)
    c: Coincident(g2,g1)
    c: Tangent(g2,g-4)
FEATURE [PartDesign::Pad] Pad011
  BaseFeature = -> Pad010
  Direction = (0,1,-2e-16)
  Length = 2.2
  Length2 = 10
  Profile = -> Sketch013
  ReferenceAxis = -> Sketch013 [N_Axis]
  Refine = true
  Reversed = true
  Suppressed = false
  Type = 0
FEATURE [Sketcher::SketchObject] Sketch014
  ArcFitTolerance = 1e-06
  AttachmentSupport = -> [Pad011]
  ExternalGeometry = -> [Pad011]
  FullyConstrained = true
  MakeInternals = false
  MapMode = 5
  Placement = pos=(0,-3,0) rot=(0,0.707107,0.707107;3.14159rad)
  sketch-geometry (3):
    g0: LineSegment StartX=1.5 StartY=2 StartZ=0 EndX=10.8 EndY=2 EndZ=0
    g1: LineSegment StartX=10.8 StartY=2 StartZ=0 EndX=10.8 EndY=5.53687 EndZ=0
    g2: ArcOfCircle CenterX=22.8718 CenterY=-40.2005 CenterZ=0 NormalX=0 NormalY=0 NormalZ=1 AngleXU=0 Radius=47.3036 StartAngle=1.82885 EndAngle=2.03958
  constraints (8):
    c: Coincident(g0,g-4)
    c: Coincident(g0,g-3)
    c: Coincident(g1,g0)
    c: Vertical(g1)
    c: PointOnObject(g1,g-4)
    c: Coincident(g2,g0)
    c: Coincident(g2,g1)
    c: Tangent(g2,g-4)
FEATURE [PartDesign::Pad] Pad012
  BaseFeature = -> Pad011
  Direction = (0,1,-2e-16)
  Length = 2.2
  Length2 = 10
  Profile = -> Sketch014
  ReferenceAxis = -> Sketch014 [N_Axis]
  Refine = true
  Reversed = true
  Suppressed = false
  Type = 0
FEATURE [Sketcher::SketchObject] Sketch015
  ArcFitTolerance = 1e-06
  AttachmentOffset = pos=(-7,0,1.8) rot=(0,0,1;0rad)
  AttachmentSupport = -> [Pad012]
  ExternalGeometry = -> [Pad012]
  FullyConstrained = true
  MakeInternals = false
  MapMode = 5
  Placement = pos=(-7,0,7.8) rot=(0,0,1;0rad)
  sketch-geometry (4):
    g0: LineSegment StartX=-17.1 StartY=5.75 StartZ=0 EndX=-17.1 EndY=-5.75 EndZ=0
    g1: LineSegment StartX=-17.1 StartY=-5.75 StartZ=0 EndX=-8 EndY=-5.75 EndZ=0
    g2: LineSegment StartX=-8 StartY=-5.75 StartZ=0 EndX=-8 EndY=5.75 EndZ=0
    g3: LineSegment StartX=-8 StartY=5.75 StartZ=0 EndX=-17.1 EndY=5.75 EndZ=0
  constraints (12):
    c: Coincident(g0,g1)
    c: Coincident(g1,g2)
    c: Coincident(g2,g3)
    c: Coincident(g3,g0)
    c: Vertical(g0)
    c: Vertical(g2)
    c: Horizontal(g1)
    c: Horizontal(g3)
    c: DistanceY(g2,g2) = 11.5
    c: DistanceY(g-1,g2) = 5.75
    c: DistanceX(g3,g3) = 9.1
    c: PointOnObject(g0,g-3)
FEATURE [PartDesign::Pad] Pad013
  BaseFeature = -> Pad012
  Direction = (0,0,1)
  Length = 0.7
  Length2 = 10
  Profile = -> Sketch015
  ReferenceAxis = -> Sketch015 [N_Axis]
  Refine = true
  Reversed = true
  Suppressed = false
  Type = 0
FEATURE [Sketcher::SketchObject] Sketch016
  ArcFitTolerance = 1e-06
  AttachmentSupport = -> [Pad013]
  ExternalGeometry = -> [Pad013]
  FullyConstrained = true
  MakeInternals = false
  MapMode = 5
  Placement = pos=(0,0,7.8) rot=(0,0,1;0rad)
  sketch-geometry (16):
    g0: LineSegment StartX=-23.1 StartY=6.55 StartZ=0 EndX=-23.1 EndY=-6.55 EndZ=0
    g1: LineSegment StartX=-24.1 StartY=6.55 StartZ=0 EndX=-24.1 EndY=-6.55 EndZ=0
    g2: ArcOfCircle CenterX=-26.0585 CenterY=9.25845 CenterZ=0 NormalX=0 NormalY=0 NormalZ=1 AngleXU=0 Radius=0.53033 StartAngle=0.785398 EndAngle=3.92699
    g3: LineSegment StartX=-26.4335 StartY=8.88345 StartZ=0 EndX=-24.1 EndY=6.55 EndZ=0
    g4: ArcOfCircle CenterX=-26.0585 CenterY=-9.25845 CenterZ=0 NormalX=0 NormalY=0 NormalZ=1 AngleXU=0 Radius=0.53033 StartAngle=2.35619 EndAngle=5.49779
    g5: LineSegment StartX=-24.1 StartY=-6.55 StartZ=0 EndX=-26.4335 EndY=-8.88345 EndZ=0
    g6: LineSegment StartX=-23.1 StartY=-6.55 StartZ=0 EndX=-19.65 EndY=-6.55 EndZ=0
    g7: ArcOfCircle CenterX=-19.65 CenterY=-7.3 CenterZ=0 NormalX=0 NormalY=0 NormalZ=1 AngleXU=0 Radius=0.75 StartAngle=4.71239 EndAngle=7.85398
    g8: LineSegment StartX=-19.65 StartY=-8.05 StartZ=0 EndX=-24.1 EndY=-8.05 EndZ=0
    g9: LineSegment StartX=-24.1 StartY=-8.05 StartZ=0 EndX=-25.6835 EndY=-9.63345 EndZ=0
    g10: LineSegment StartX=-23.1 StartY=6.55 StartZ=0 EndX=-19.65 EndY=6.55 EndZ=0
    g11: ArcOfCircle CenterX=-19.65 CenterY=7.3 CenterZ=0 NormalX=0 NormalY=0 NormalZ=1 AngleXU=0 Radius=0.75 StartAngle=4.71239 EndAngle=7.85398
    g12: LineSegment StartX=-19.65 StartY=8.05 StartZ=0 EndX=-24.1 EndY=8.05 EndZ=0
    g13: LineSegment StartX=-24.1 StartY=8.05 StartZ=0 EndX=-25.6835 EndY=9.63345 EndZ=0
    g14: LineSegment [constr] StartX=-26.4335 StartY=8.88345 StartZ=0 EndX=-25.6835 EndY=9.63345 EndZ=0
    g15: LineSegment [constr] StartX=-25.6835 StartY=-9.63345 StartZ=0 EndX=-26.4335 EndY=-8.88345 EndZ=0
  constraints (51):
    c: Vertical(g0)
    c: PointOnObject(g1,g-3)
    c: PointOnObject(g1,g-3)
    c: Coincident(g3,g1)
    c: Coincident(g5,g1)
    c: Coincident(g5,g4)
    c: Coincident(g6,g0)
    c: Horizontal(g6)
    c: Coincident(g7,g6)
    c: Coincident(g8,g7)
    c: Horizontal(g8)
    c: Coincident(g9,g8)
    c: Coincident(g9,g4)
    c: Coincident(g10,g0)
    c: Horizontal(g10)
    c: Coincident(g11,g10)
    c: Coincident(g12,g11)
    c: Horizontal(g12)
    c: Coincident(g13,g12)
    c: Coincident(g2,g13)
    c: Coincident(g3,g2)
    c: Angle(g1,g5) = 2.35619
    c: Parallel(g5,g9)
    c: Parallel(g13,g3)
    c: Angle(g3,g1) = 2.35619
    c: Diameter(g7) = 1.5
    c: Diameter(g11) = 1.5
    c: DistanceX(g11,g11) = 0
    c: DistanceX(g11,g10) = 0
    c: DistanceX(g7,g6) = 0
    c: DistanceX(g7,g7) = 0
    c: DistanceX(g-5,g-5) = 0
    c: DistanceX(g1,g0) = 1
    c: DistanceY(g11,g-6) = 1
    c: DistanceY(g-7,g7) = 1
    c: DistanceY(g0,g1) = 0
    c: DistanceX(g0,g7) = 3.45
    c: DistanceX(g0,g10) = 3.45
    c: DistanceX(g8,g1) = 0
    c: DistanceX(g12,g1) = 0
    c: DistanceY(g1,g0) = 0
    c: Distance(g5) = 3.3
    c: Distance(g3) = 3.3
    c: Coincident(g14,g2)
    c: Coincident(g14,g2)
    c: PointOnObject(g2,g14)
    c: Coincident(g15,g4)
    c: Coincident(g15,g4)
    c: PointOnObject(g4,g15)
    c: Angle(g15,g5) = 1.5708
    c: Angle(g3,g14) = 1.5708
FEATURE [PartDesign::Pad] Pad014
  BaseFeature = -> Pad013
  Direction = (0,0,1)
  Length = 2
  Length2 = 10
  Profile = -> Sketch016
  ReferenceAxis = -> Sketch016 [N_Axis]
  Refine = true
  Reversed = true
  Suppressed = false
  Type = 0
FEATURE [Sketcher::SketchObject] Sketch017
  ArcFitTolerance = 1e-06
  AttachmentSupport = -> [Pad014]
  ExternalGeometry = -> [Pad014]
  FullyConstrained = true
  MakeInternals = false
  MapMode = 5
  Placement = pos=(-4.4698e-12,-7.55,-1.265e-12) rot=(0,0.707107,0.707107;3.14159rad)
  sketch-geometry (4):
    g0: ArcOfCircle CenterX=22.8718 CenterY=-40.2005 CenterZ=0 NormalX=0 NormalY=0 NormalZ=1 AngleXU=0 Radius=47.2964 StartAngle=1.57654 EndAngle=1.67398
    g1: LineSegment StartX=18 StartY=6.84432 StartZ=0 EndX=18 EndY=4.5 EndZ=0
    g2: LineSegment StartX=18 StartY=4.5 StartZ=0 EndX=22.6 EndY=4.5 EndZ=0
    g3: LineSegment StartX=22.6 StartY=4.5 StartZ=0 EndX=22.6 EndY=7.09512 EndZ=0
  constraints (10):
    c: Coincident(g0,g-5)
    c: Coincident(g0,g-4)
    c: Tangent(g0,g-7)
    c: Coincident(g1,g-5)
    c: PointOnObject(g1,g-5)
    c: Coincident(g2,g1)
    c: Coincident(g2,g-6)
    c: Horizontal(g2)
    c: Coincident(g3,g2)
    c: Coincident(g3,g0)
FEATURE [PartDesign::Pocket] Pocket003
  BaseFeature = -> Pad014
  Direction = (-5.92e-13,-1,-1.675e-13)
  Length = 15.1
  Length2 = 5
  Profile = -> Sketch017
  ReferenceAxis = -> Sketch017 [N_Axis]
  Refine = true
  Reversed = true
  Suppressed = false
  Type = 0
FEATURE [Sketcher::SketchObject] Sketch018
  ArcFitTolerance = 1e-06
  AttachmentSupport = -> [Pocket003]
  ExternalGeometry = -> [Pocket003]
  FullyConstrained = true
  MakeInternals = false
  MapMode = 5
  Placement = pos=(0,0,7.8) rot=(0,0,1;0rad)
  sketch-geometry (8):
    g0: LineSegment StartX=-23.1 StartY=-6.55 StartZ=0 EndX=-19.65 EndY=-6.55 EndZ=0
    g1: ArcOfCircle CenterX=-19.65 CenterY=-7.3 CenterZ=0 NormalX=0 NormalY=0 NormalZ=1 AngleXU=0 Radius=0.75 StartAngle=4.7124 EndAngle=7.85397
    g2: LineSegment StartX=-19.65 StartY=-8.05 StartZ=0 EndX=-24.1 EndY=-8.05 EndZ=0
    g3: LineSegment StartX=-24.1 StartY=-8.05 StartZ=0 EndX=-23.1 EndY=-6.55 EndZ=0
    g4: LineSegment StartX=-24.1 StartY=8.05 StartZ=0 EndX=-19.65 EndY=8.05 EndZ=0
    g5: LineSegment StartX=-24.1 StartY=8.05 StartZ=0 EndX=-23.1 EndY=6.55 EndZ=0
    g6: LineSegment StartX=-23.1 StartY=6.55 StartZ=0 EndX=-19.65 EndY=6.55 EndZ=0
    g7: ArcOfCircle CenterX=-19.65 CenterY=7.3 CenterZ=0 NormalX=0 NormalY=0 NormalZ=1 AngleXU=0 Radius=0.75 StartAngle=4.71239 EndAngle=7.85398
  constraints (18):
    c: Coincident(g0,g-7)
    c: Coincident(g0,g-8)
    c: Coincident(g1,g0)
    c: Coincident(g1,g-9)
    c: Tangent(g1,g-8)
    c: Coincident(g3,g2)
    c: Coincident(g3,g0)
    c: Coincident(g2,g-9)
    c: Coincident(g2,g1)
    c: Coincident(g4,g-3)
    c: Coincident(g4,g-6)
    c: Coincident(g5,g4)
    c: Coincident(g5,g-5)
    c: Coincident(g6,g5)
    c: Coincident(g6,g-6)
    c: Coincident(g7,g4)
    c: Coincident(g7,g6)
    c: Tangent(g7,g-6)
FEATURE [PartDesign::Pad] Pad015
  BaseFeature = -> Pocket003
  Direction = (0,0,1)
  Length = 6
  Length2 = 10
  Profile = -> Sketch018
  ReferenceAxis = -> Sketch018 [N_Axis]
  Refine = true
  Suppressed = false
  Type = 0
FEATURE [Sketcher::SketchObject] Sketch019
  ArcFitTolerance = 1e-06
  AttachmentSupport = -> [Pad015]
  ExternalGeometry = -> [Pad015]
  FullyConstrained = true
  MakeInternals = false
  MapMode = 5
  Placement = pos=(0,0,7.8) rot=(0,0,1;0rad)
  sketch-geometry (10):
    g0: LineSegment StartX=-23.1 StartY=-6.55 StartZ=0 EndX=-23.1 EndY=6.55 EndZ=0
    g1: LineSegment StartX=-23.1 StartY=6.55 StartZ=0 EndX=-24.1 EndY=8.05 EndZ=0
    g2: LineSegment StartX=-24.1 StartY=8.05 StartZ=0 EndX=-25.6835 EndY=9.63345 EndZ=0
    g3: ArcOfCircle CenterX=-26.0584 CenterY=9.25845 CenterZ=0 NormalX=0 NormalY=0 NormalZ=1 AngleXU=0 Radius=0.53033 StartAngle=0.785412 EndAngle=3.92698
    g4: LineSegment StartX=-26.4335 StartY=8.88345 StartZ=0 EndX=-24.1 EndY=6.55 EndZ=0
    g5: LineSegment StartX=-24.1 StartY=6.55 StartZ=0 EndX=-24.1 EndY=-6.55 EndZ=0
    g6: LineSegment StartX=-23.1 StartY=-6.55 StartZ=0 EndX=-24.1 EndY=-8.05 EndZ=0
    g7: LineSegment StartX=-24.1 StartY=-8.05 StartZ=0 EndX=-25.6835 EndY=-9.63345 EndZ=0
    g8: LineSegment StartX=-24.1 StartY=-6.55 StartZ=0 EndX=-26.4335 EndY=-8.88345 EndZ=0
    g9: ArcOfCircle CenterX=-26.0585 CenterY=-9.25845 CenterZ=0 NormalX=0 NormalY=0 NormalZ=1 AngleXU=0 Radius=0.53033 StartAngle=2.35619 EndAngle=5.49779
  constraints (22):
    c: Coincident(g0,g-10)
    c: Coincident(g0,g-4)
    c: Coincident(g1,g0)
    c: Coincident(g1,g-5)
    c: Coincident(g2,g-4)
    c: Coincident(g2,g-6)
    c: Coincident(g3,g2)
    c: Coincident(g3,g-7)
    c: Tangent(g3,g-6)
    c: Coincident(g4,g3)
    c: Coincident(g4,g-8)
    c: Coincident(g5,g4)
    c: Coincident(g5,g-13)
    c: Coincident(g6,g0)
    c: Coincident(g6,g-11)
    c: Coincident(g7,g6)
    c: Coincident(g7,g-12)
    c: Coincident(g8,g5)
    c: Coincident(g8,g-13)
    c: Coincident(g9,g8)
    c: Coincident(g9,g7)
    c: Tangent(g9,g-12)
FEATURE [PartDesign::Pad] Pad016
  BaseFeature = -> Pad015
  Direction = (0,0,1)
  Length = 7
  Length2 = 10
  Profile = -> Sketch019
  ReferenceAxis = -> Sketch019 [N_Axis]
  Refine = true
  Suppressed = false
  Type = 0
FEATURE [Sketcher::SketchObject] Sketch020
  ArcFitTolerance = 1e-06
  AttachmentSupport = -> [Pad016]
  ExternalGeometry = -> [Pad016]
  FullyConstrained = true
  MakeInternals = false
  MapMode = 5
  Placement = pos=(0,0,7.8) rot=(0,0,1;0rad)
  sketch-geometry (10):
    g0: LineSegment StartX=-13.6 StartY=-5.75 StartZ=0 EndX=-18.9 EndY=-5.75 EndZ=0
    g1: LineSegment StartX=-18.9 StartY=-5.75 StartZ=0 EndX=-18.9 EndY=-6.55 EndZ=0
    g2: LineSegment StartX=-18.9 StartY=-6.55 StartZ=0 EndX=-17 EndY=-8.05 EndZ=0
    g3: LineSegment StartX=-17 StartY=-8.05 StartZ=0 EndX=-13.6 EndY=-8.05 EndZ=0
    g4: LineSegment StartX=-13.6 StartY=-5.75 StartZ=0 EndX=-13.6 EndY=-8.05 EndZ=0
    g5: LineSegment StartX=-18.9 StartY=5.75 StartZ=0 EndX=-18.9 EndY=6.55 EndZ=0
    g6: LineSegment StartX=-18.9 StartY=6.55 StartZ=0 EndX=-17 EndY=8.05 EndZ=0
    g7: LineSegment StartX=-17 StartY=8.05 StartZ=0 EndX=-13.6 EndY=8.05 EndZ=0
    g8: LineSegment StartX=-13.6 StartY=8.05 StartZ=0 EndX=-13.6 EndY=5.75 EndZ=0
    g9: LineSegment StartX=-13.6 StartY=5.75 StartZ=0 EndX=-18.9 EndY=5.75 EndZ=0
  constraints (31):
    c: Horizontal(g0)
    c: Coincident(g1,g0)
    c: Vertical(g1)
    c: Coincident(g2,g1)
    c: Coincident(g3,g2)
    c: Horizontal(g3)
    c: Coincident(g4,g0)
    c: Coincident(g4,g3)
    c: Vertical(g4)
    c: Vertical(g5)
    c: Coincident(g6,g5)
    c: Coincident(g7,g6)
    c: Horizontal(g7)
    c: Coincident(g8,g7)
    c: Vertical(g8)
    c: Coincident(g9,g8)
    c: Coincident(g9,g5)
    c: Horizontal(g9)
    c: PointOnObject(g5,g-3)
    c: DistanceX(g0,g0) = 5.3
    c: DistanceX(g9,g9) = 5.3
    c: DistanceY(g8,g8) = 2.3
    c: DistanceY(g4,g4) = 2.3
    c: PointOnObject(g0,g-4)
    c: Radius(g-6) = 0.75
    c: DistanceX(g-6,g5) = 0.75
    c: DistanceY(g5,g-6) = 0
    c: DistanceY(g1,g-5) = 0
    c: DistanceX(g-5,g1) = 0.75
    c: PointOnObject(g6,g-7)
    c: PointOnObject(g2,g-7)
FEATURE [PartDesign::Pocket] Pocket004
  BaseFeature = -> Pad016
  Direction = (0,0,-1)
  Length = 5
  Length2 = 5
  Profile = -> Sketch020
  ReferenceAxis = -> Sketch020 [N_Axis]
  Refine = true
  Suppressed = false
  Type = 0
FEATURE [Sketcher::SketchObject] Sketch021
  ArcFitTolerance = 1e-06
  AttachmentSupport = -> [Pocket004]
  ExternalGeometry = -> [Pocket004]
  FullyConstrained = true
  MakeInternals = false
  MapMode = 5
  Placement = pos=(0,0,0) rot=(1,0,0;3.14159rad)
  sketch-geometry (4):
    g0: Circle CenterX=-2 CenterY=-9.99098 CenterZ=0 NormalX=0 NormalY=0 NormalZ=1 AngleXU=0 Radius=0.75
    g1: Circle CenterX=-26.1 CenterY=-10.991 CenterZ=0 NormalX=0 NormalY=0 NormalZ=1 AngleXU=0 Radius=0.75
    g2: Circle CenterX=-26.1 CenterY=10.991 CenterZ=0 NormalX=0 NormalY=0 NormalZ=1 AngleXU=0 Radius=0.75
    g3: Circle CenterX=-2 CenterY=9.99098 CenterZ=0 NormalX=0 NormalY=0 NormalZ=1 AngleXU=0 Radius=0.75
  constraints (16):
    c: Diameter(g3) = 1.5
    c: Diameter(g0) = 1.5
    c: Diameter(g1) = 1.5
    c: Diameter(g2) = 1.5
    c: PointOnObject(g-3,g2)
    c: PointOnObject(g-5,g3)
    c: PointOnObject(g-6,g0)
    c: PointOnObject(g-4,g1)
    c: DistanceX(g-4,g-7) = 1.5
    c: DistanceX(g-6,g-8) = 1.5
    c: DistanceX(g-5,g-8) = 1.5
    c: DistanceX(g-3,g-9) = 1.5
    c: DistanceX(g2,g-9) = 2
    c: DistanceX(g1,g-7) = 2
    c: DistanceX(g0,g-8) = 2
    c: DistanceX(g3,g-8) = 2
FEATURE [PartDesign::Pad] Pad017
  BaseFeature = -> Pocket004
  Direction = (0,0,-1)
  Length = 1.25
  Length2 = 10
  Profile = -> Sketch021
  ReferenceAxis = -> Sketch021 [N_Axis]
  Refine = true
  Suppressed = false
  Type = 0
FEATURE [PartDesign::Fillet] Fillet
  Base = -> Pad017 [Edge111,Edge203,Edge205,Edge113]
  BaseFeature = -> Pad017
  Radius = 0.5
  Refine = true
  SupportTransform = false
  Suppressed = false
  UseAllEdges = false
FEATURE [PartDesign::Body] Body  label="Rear_Torso"
  AllowCompound = false
  Group = -> [Sketch,Pad,Sketch001,Pad001,Sketch002,Pocket,Sketch003,Pocket001,Sketch004,Pad002,Sketch005,Pad003,Sketch006,Pocket002,Sketch007,Pad004,Sketch008,Pad005,Sketch009,Pad006,Sketch010,Pad007,Pad008,Sketch011,Pad009,Sketch012,Pad010,Sketch013,Pad011,Sketch014,Pad012,Sketch015,Pad013,Sketch016,Pad014,Sketch017,Pocket003,Sketch018,Pad015,Sketch019,Pad016,Sketch020,Pocket004,Sketch021,Pad017,Fillet,+55 more]
  Origin = -> Origin
  Tip = -> Pocket142
COMPONENT P1 — recipe-attached ("Front_Torso", modeled in this document).
Construction recipe (the document's own serialized feature program — sketch geometry with constraints, then the solid features built on it; lengths are millimeters unless a unit is written):

FEATURE [PartDesign::SubShapeBinder] Binder
  BindCopyOnChange = 0
  BindMode = 2
  ClaimChildren = false
  Context = -> Body001 [Binder.]
  Fuse = false
  MakeFace = true
  OffsetFill = false
  OffsetIntersection = false
  OffsetJoinType = 0
  OffsetOpenResult = false
  PartialLoad = false
  Refine = true
  Relative = true
  _Version = 2
FEATURE [PartDesign::Pad] Pad025
  Direction = (0,0,-1)
  Length = 7.5
  Length2 = 10
  Profile = -> Binder
  Refine = true
  Suppressed = false
  Type = 0
FEATURE [Sketcher::SketchObject] Sketch044
  ArcFitTolerance = 1e-06
  AttachmentSupport = -> [Pad025]
  ExternalGeometry = -> [Pad025]
  FullyConstrained = true
  MakeInternals = false
  MapMode = 5
  Placement = pos=(0,0,-7.5) rot=(1,0,0;3.14159rad)
  sketch-geometry (22):
    g0: LineSegment StartX=-30.2458 StartY=12.808 StartZ=0 EndX=-35.5518 EndY=4 EndZ=0
    g1: LineSegment StartX=-30.2458 StartY=-12.808 StartZ=0 EndX=-35.5518 EndY=-4 EndZ=0
    g2: LineSegment StartX=-35.5518 StartY=4 StartZ=0 EndX=-35.5518 EndY=-4 EndZ=0
    g3: ArcOfCircle CenterX=-29.8175 CenterY=-12.55 CenterZ=0 NormalX=0 NormalY=0 NormalZ=1 AngleXU=0 Radius=0.5 StartAngle=3.68378 EndAngle=4.71239
    g4: ArcOfCircle CenterX=-24.6 CenterY=-12.55 CenterZ=0 NormalX=0 NormalY=0 NormalZ=1 AngleXU=0 Radius=0.5 StartAngle=4.71239 EndAngle=6.28319
    g5: LineSegment StartX=-29.8175 StartY=-13.05 StartZ=0 EndX=-24.6 EndY=-13.05 EndZ=0
    g6: LineSegment StartX=-24.1 StartY=-12.55 StartZ=0 EndX=-24.1 EndY=-9.05 EndZ=0
    g7: LineSegment StartX=-24.1 StartY=-9.05 StartZ=0 EndX=-18.5 EndY=-9.05 EndZ=0
    g8: ArcOfCircle CenterX=-18 CenterY=-12.55 CenterZ=0 NormalX=0 NormalY=0 NormalZ=1 AngleXU=0 Radius=0.5 StartAngle=3.14159 EndAngle=4.71239
    g9: LineSegment StartX=-18 StartY=-13.05 StartZ=0 EndX=-0.5 EndY=-13.05 EndZ=0
    g10: LineSegment StartX=-18.5 StartY=-9.05 StartZ=0 EndX=-18.5 EndY=-12.55 EndZ=0
    g11: ArcOfCircle CenterX=-29.8175 CenterY=12.55 CenterZ=0 NormalX=0 NormalY=0 NormalZ=1 AngleXU=0 Radius=0.5 StartAngle=1.5708 EndAngle=2.5994
    g12: LineSegment StartX=-29.8175 StartY=13.05 StartZ=0 EndX=-24.6 EndY=13.05 EndZ=0
    g13: ArcOfCircle CenterX=-24.6 CenterY=12.55 CenterZ=0 NormalX=0 NormalY=0 NormalZ=1 AngleXU=0 Radius=0.5 StartAngle=-9.24e-14 EndAngle=1.5708
    g14: LineSegment StartX=-24.1 StartY=12.55 StartZ=0 EndX=-24.1 EndY=9.05 EndZ=0
    g15: LineSegment StartX=-24.1 StartY=9.05 StartZ=0 EndX=-18.5 EndY=9.05 EndZ=0
    g16: LineSegment StartX=-18.5 StartY=9.05 StartZ=0 EndX=-18.5 EndY=12.55 EndZ=0
    g17: ArcOfCircle CenterX=-18 CenterY=12.55 CenterZ=0 NormalX=0 NormalY=0 NormalZ=1 AngleXU=0 Radius=0.5 StartAngle=1.5708 EndAngle=3.14159
    g18: LineSegment StartX=-18 StartY=13.05 StartZ=0 EndX=-0.5 EndY=13.05 EndZ=0
    g19: ArcOfCircle CenterX=-0.5 CenterY=12.55 CenterZ=0 NormalX=0 NormalY=0 NormalZ=1 AngleXU=0 Radius=0.5 StartAngle=-1.07e-14 EndAngle=1.5708
    g20: ArcOfCircle CenterX=-0.499996 CenterY=-12.55 CenterZ=0 NormalX=0 NormalY=0 NormalZ=1 AngleXU=0 Radius=0.499996 StartAngle=4.71238 EndAngle=6.28319
    g21: LineSegment StartX=-1.92553e-11 StartY=-12.55 StartZ=0 EndX=1e-16 EndY=12.55 EndZ=0
  constraints (49):
    c: Coincident(g0,g-27)
    c: PointOnObject(g-27,g0)
    c: Coincident(g1,g-8)
    c: PointOnObject(g-7,g1)
    c: Coincident(g2,g0)
    c: Coincident(g2,g1)
    c: Vertical(g2)
    c: Coincident(g3,g1)
    c: Coincident(g3,g-9)
    c: Tangent(g4,g-10) = -1.5708
    c: Coincident(g4,g-11)
    c: DistanceY(g2,g2) = 8
    c: Coincident(g5,g3)
    c: Coincident(g5,g4)
    c: Coincident(g6,g4)
    c: Coincident(g6,g-12)
    c: Coincident(g7,g6)
    c: Coincident(g7,g-13)
    c: Coincident(g8,g-15)
    c: Coincident(g-14,g8)
    c: Coincident(g9,g-16)
    c: Coincident(g9,g8)
    c: DistanceY(g8,g8) = 0
    c: Coincident(g10,g7)
    c: Coincident(g10,g8)
    c: Tangent(g3,g-8)
    c: Coincident(g11,g0)
    c: Tangent(g11,g-26) = -1.5708
    c: Coincident(g12,g11)
    c: Coincident(g12,g-25)
    c: Coincident(g13,g12)
    c: Tangent(g13,g-24) = -1.5708
    c: Coincident(g14,g13)
    c: Coincident(g14,g-23)
    c: Coincident(g15,g14)
    c: Coincident(g15,g-22)
    c: Coincident(g16,g-21)
    c: Coincident(g16,g15)
    c: Coincident(g17,g16)
    c: Tangent(g17,g-20) = -1.5708
    c: Coincident(g18,g17)
    c: Coincident(g18,g-19)
    c: Coincident(g19,g18)
    c: Tangent(g19,g-18) = -1.5708
    c: Coincident(g20,g9)
    c: Coincident(g20,g-17)
    c: Tangent(g20,g-16)
    c: Coincident(g21,g19)
    c: Coincident(g21,g20)
FEATURE [PartDesign::Pad] Pad026
  BaseFeature = -> Pad025
  Direction = (0,0,-1)
  Length = 1.5
  Length2 = 10
  Profile = -> Sketch044
  ReferenceAxis = -> Sketch044 [N_Axis]
  Refine = true
  Reversed = true
  Suppressed = false
  Type = 0
FEATURE [Sketcher::SketchObject] Sketch045
  ArcFitTolerance = 1e-06
  AttachmentSupport = -> [Pad026]
  ExternalGeometry = -> [Pad026]
  FullyConstrained = true
  MakeInternals = false
  MapMode = 5
  Placement = pos=(0,0,-7.5) rot=(1,0,0;3.14159rad)
  sketch-geometry (4):
    g0: LineSegment StartX=-24.1 StartY=9.05 StartZ=0 EndX=-24.1 EndY=-9.05 EndZ=0
    g1: LineSegment StartX=-24.1 StartY=-9.05 StartZ=0 EndX=-18.5 EndY=-9.05 EndZ=0
    g2: LineSegment StartX=-18.5 StartY=-9.05 StartZ=0 EndX=-18.5 EndY=9.05 EndZ=0
    g3: LineSegment StartX=-18.5 StartY=9.05 StartZ=0 EndX=-24.1 EndY=9.05 EndZ=0
  constraints (10):
    c: Coincident(g0,g1)
    c: Coincident(g1,g2)
    c: Coincident(g2,g3)
    c: Coincident(g3,g0)
    c: Vertical(g0)
    c: Vertical(g2)
    c: Horizontal(g1)
    c: Horizontal(g3)
    c: Coincident(g0,g-3)
    c: Coincident(g1,g-4)
FEATURE [PartDesign::Pocket] Pocket021
  BaseFeature = -> Pad026
  Direction = (0,0,1)
  Length = 1.5
  Length2 = 5
  Profile = -> Sketch045
  ReferenceAxis = -> Sketch045 [N_Axis]
  Refine = true
  Suppressed = false
  Type = 0
FEATURE [Sketcher::SketchObject] Sketch046
  ArcFitTolerance = 1e-06
  AttachmentSupport = -> [Pocket021]
  ExternalGeometry = -> [Pocket021]
  FullyConstrained = true
  MakeInternals = false
  MapMode = 5
  Placement = pos=(0,0,-6) rot=(0,0,1;0rad)
  sketch-geometry (4):
    g0: LineSegment StartX=-35.5518 StartY=3.1 StartZ=0 EndX=-35.5518 EndY=-3.1 EndZ=0
    g1: LineSegment StartX=-35.5518 StartY=-3.1 StartZ=0 EndX=-34.0518 EndY=-3.1 EndZ=0
    g2: LineSegment StartX=-34.0518 StartY=-3.1 StartZ=0 EndX=-34.0518 EndY=3.1 EndZ=0
    g3: LineSegment StartX=-34.0518 StartY=3.1 StartZ=0 EndX=-35.5518 EndY=3.1 EndZ=0
  constraints (12):
    c: Coincident(g0,g1)
    c: Coincident(g1,g2)
    c: Coincident(g2,g3)
    c: Coincident(g3,g0)
    c: Vertical(g0)
    c: Vertical(g2)
    c: Horizontal(g1)
    c: Horizontal(g3)
    c: PointOnObject(g0,g-3)
    c: DistanceX(g3,g3) = 1.5
    c: DistanceY(g0,g0) = 6.2
    c: DistanceY(g-1,g0) = 3.1
FEATURE [PartDesign::Pad] Pad027
  BaseFeature = -> Pocket021
  Direction = (0,0,1)
  Length = 6
  Length2 = 10
  Profile = -> Sketch046
  ReferenceAxis = -> Sketch046 [N_Axis]
  Refine = true
  Suppressed = false
  Type = 0
FEATURE [Sketcher::SketchObject] Sketch047
  ArcFitTolerance = 1e-06
  AttachmentSupport = -> [Pad027]
  ExternalGeometry = -> [Pad027]
  FullyConstrained = true
  MakeInternals = false
  MapMode = 5
  Placement = pos=(0,0,-6) rot=(0,0,1;0rad)
  sketch-geometry (12):
    g0: LineSegment StartX=-35.5518 StartY=3.1 StartZ=0 EndX=-35.5518 EndY=4 EndZ=0
    g1: LineSegment StartX=-35.5518 StartY=4 StartZ=0 EndX=-32.6 EndY=8.9 EndZ=0
    g2: LineSegment StartX=-32.6 StartY=8.9 StartZ=0 EndX=-30.8664 EndY=8.9 EndZ=0
    g3: LineSegment StartX=-30.8664 StartY=8.9 StartZ=0 EndX=-34.0518 EndY=3.6122 EndZ=0
    g4: LineSegment StartX=-35.5518 StartY=3.1 StartZ=0 EndX=-34.0518 EndY=3.1 EndZ=0
    g5: LineSegment StartX=-34.0518 StartY=3.1 StartZ=0 EndX=-34.0518 EndY=3.6122 EndZ=0
    g6: LineSegment StartX=-34.0518 StartY=-3.1 StartZ=0 EndX=-35.5518 EndY=-3.1 EndZ=0
    g7: LineSegment StartX=-35.5518 StartY=-3.1 StartZ=0 EndX=-35.5518 EndY=-4 EndZ=0
    g8: LineSegment StartX=-35.5518 StartY=-4 StartZ=0 EndX=-32.6 EndY=-8.9 EndZ=0
    g9: LineSegment StartX=-32.6 StartY=-8.9 StartZ=0 EndX=-30.8664 EndY=-8.9 EndZ=0
    g10: LineSegment StartX=-30.8664 StartY=-8.9 StartZ=0 EndX=-34.0518 EndY=-3.6122 EndZ=0
    g11: LineSegment StartX=-34.0518 StartY=-3.1 StartZ=0 EndX=-34.0518 EndY=-3.6122 EndZ=0
  constraints (26):
    c: Coincident(g0,g-6)
    c: Coincident(g0,g-5)
    c: Coincident(g1,g0)
    c: Coincident(g1,g-4)
    c: Coincident(g2,g1)
    c: Coincident(g2,g-3)
    c: Coincident(g3,g2)
    c: Coincident(g4,g0)
    c: Coincident(g4,g-6)
    c: Coincident(g5,g4)
    c: Coincident(g5,g3)
    c: Vertical(g5)
    c: Parallel(g1,g3)
    c: Coincident(g6,g-7)
    c: Coincident(g6,g-8)
    c: Coincident(g7,g6)
    c: Coincident(g7,g-9)
    c: Coincident(g8,g7)
    c: Coincident(g8,g-10)
    c: Coincident(g9,g8)
    c: Coincident(g9,g-10)
    c: Coincident(g10,g9)
    c: Coincident(g11,g6)
    c: Coincident(g11,g10)
    c: Vertical(g11)
    c: Parallel(g8,g10)
FEATURE [PartDesign::Pad] Pad028
  BaseFeature = -> Pad027
  Direction = (0,0,1)
  Length = 1
  Length2 = 10
  Profile = -> Sketch047
  ReferenceAxis = -> Sketch047 [N_Axis]
  Refine = true
  Suppressed = false
  Type = 0
FEATURE [Sketcher::SketchObject] Sketch048
  ArcFitTolerance = 1e-06
  AttachmentSupport = -> [Pad028]
  ExternalGeometry = -> [Pad028]
  FullyConstrained = true
  MakeInternals = false
  MapMode = 5
  sketch-geometry (4):
    g0: LineSegment StartX=-1.5 StartY=3 StartZ=0 EndX=-1.5 EndY=-3 EndZ=0
    g1: LineSegment StartX=-1.5 StartY=-3 StartZ=0 EndX=0 EndY=-3 EndZ=0
    g2: LineSegment StartX=0 StartY=-3 StartZ=0 EndX=0 EndY=3 EndZ=0
    g3: LineSegment StartX=0 StartY=3 StartZ=0 EndX=-1.5 EndY=3 EndZ=0
  constraints (10):
    c: Coincident(g0,g1)
    c: Coincident(g1,g2)
    c: Coincident(g2,g3)
    c: Coincident(g3,g0)
    c: Vertical(g2)
    c: Horizontal(g1)
    c: Horizontal(g3)
    c: Coincident(g0,g-4)
    c: PointOnObject(g1,g-3)
    c: Coincident(g0,g-4)
FEATURE [PartDesign::Pocket] Pocket022
  BaseFeature = -> Pad028
  Direction = (0,0,-1)
  Length = 5.3
  Length2 = 5
  Profile = -> Sketch048
  ReferenceAxis = -> Sketch048 [N_Axis]
  Refine = true
  Suppressed = false
  Type = 0
FEATURE [Sketcher::SketchObject] Sketch049
  ArcFitTolerance = 1e-06
  AttachmentSupport = -> [Pocket022]
  ExternalGeometry = -> [Pocket022]
  FullyConstrained = true
  MakeInternals = false
  MapMode = 5
  Placement = pos=(0,0,-6) rot=(0,0,1;0rad)
  sketch-geometry (4):
    g0: LineSegment StartX=-34.0518 StartY=2.5 StartZ=0 EndX=-34.0518 EndY=-2.5 EndZ=0
    g1: LineSegment StartX=-34.0518 StartY=-2.5 StartZ=0 EndX=-1.5 EndY=-2.5 EndZ=0
    g2: LineSegment StartX=-1.5 StartY=-2.5 StartZ=0 EndX=-1.5 EndY=2.5 EndZ=0
    g3: LineSegment StartX=-1.5 StartY=2.5 StartZ=0 EndX=-34.0518 EndY=2.5 EndZ=0
  constraints (12):
    c: Coincident(g0,g1)
    c: Coincident(g1,g2)
    c: Coincident(g2,g3)
    c: Coincident(g3,g0)
    c: Vertical(g0)
    c: Vertical(g2)
    c: Horizontal(g1)
    c: Horizontal(g3)
    c: PointOnObject(g0,g-4)
    c: PointOnObject(g1,g-3)
    c: DistanceY(g-1,g2) = 2.5
    c: DistanceY(g1,g-1) = 2.5
FEATURE [PartDesign::Pocket] Pocket023
  BaseFeature = -> Pocket022
  Direction = (0,0,-1)
  Length = 5
  Length2 = 5
  Profile = -> Sketch049
  ReferenceAxis = -> Sketch049 [N_Axis]
  Refine = true
  Suppressed = false
  Type = 0
FEATURE [Sketcher::SketchObject] Sketch050
  ArcFitTolerance = 1e-06
  AttachmentSupport = -> [Pocket023]
  ExternalGeometry = -> [Pocket023]
  FullyConstrained = true
  MakeInternals = false
  MapMode = 5
  sketch-geometry (12):
    g0: ArcOfCircle CenterX=-0.5 CenterY=-12.55 CenterZ=0 NormalX=0 NormalY=0 NormalZ=1 AngleXU=0 Radius=0.5 StartAngle=4.71239 EndAngle=6.28319
    g1: ArcOfCircle CenterX=-18 CenterY=-12.55 CenterZ=0 NormalX=0 NormalY=0 NormalZ=1 AngleXU=0 Radius=0.5 StartAngle=3.14159 EndAngle=4.71239
    g2: ArcOfCircle CenterX=-18 CenterY=12.55 CenterZ=0 NormalX=0 NormalY=0 NormalZ=1 AngleXU=0 Radius=0.5 StartAngle=1.5708 EndAngle=3.14159
    g3: ArcOfCircle CenterX=-0.5 CenterY=12.55 CenterZ=0 NormalX=0 NormalY=0 NormalZ=1 AngleXU=0 Radius=0.5 StartAngle=2e-16 EndAngle=1.5708
    g4: LineSegment StartX=-0.5 StartY=13.05 StartZ=0 EndX=0 EndY=13.05 EndZ=0
    g5: LineSegment StartX=1e-16 StartY=12.55 StartZ=0 EndX=0 EndY=13.05 EndZ=0
    g6: LineSegment StartX=-18.5 StartY=12.55 StartZ=0 EndX=-18.5 EndY=13.05 EndZ=0
    g7: LineSegment StartX=-18 StartY=13.05 StartZ=0 EndX=-18.5 EndY=13.05 EndZ=0
    g8: LineSegment StartX=-18 StartY=-13.05 StartZ=0 EndX=-18.5 EndY=-13.05 EndZ=0
    g9: LineSegment StartX=-18.5 StartY=-12.55 StartZ=0 EndX=-18.5 EndY=-13.05 EndZ=0
    g10: LineSegment StartX=-2.35e-14 StartY=-12.55 StartZ=0 EndX=0 EndY=-13.05 EndZ=0
    g11: LineSegment StartX=-0.5 StartY=-13.05 StartZ=0 EndX=0 EndY=-13.05 EndZ=0
  constraints (27):
    c: Tangent(g0,g-6) = -1.5708
    c: Coincident(g0,g-6)
    c: Tangent(g1,g-5) = -1.5708
    c: Coincident(g1,g-5)
    c: Tangent(g2,g-4) = -1.5708
    c: Coincident(g2,g-4)
    c: Tangent(g3,g-3) = -1.5708
    c: Coincident(g3,g-3)
    c: Coincident(g4,g3)
    c: PointOnObject(g4,g-2)
    c: Horizontal(g4)
    c: Coincident(g5,g3)
    c: Coincident(g5,g4)
    c: Tangent(g6,g2) = 1.5708
    c: Horizontal(g7)
    c: Coincident(g6,g7)
    c: Coincident(g7,g2)
    c: Coincident(g8,g1)
    c: Horizontal(g8)
    c: Coincident(g9,g1)
    c: Coincident(g9,g8)
    c: Vertical(g9)
    c: Coincident(g10,g0)
    c: PointOnObject(g10,g-2)
    c: Coincident(g11,g0)
    c: Coincident(g11,g10)
    c: Horizontal(g11)
FEATURE [PartDesign::Pad] Pad029
  BaseFeature = -> Pocket023
  Direction = (0,0,1)
  Length = 7.5
  Length2 = 10
  Profile = -> Sketch050
  ReferenceAxis = -> Sketch050 [N_Axis]
  Refine = true
  Reversed = true
  Suppressed = false
  Type = 0
FEATURE [PartDesign::Pocket] Pocket024
  BaseFeature = -> Pad029
  Direction = (0,1,0)
  Length = 1
  Length2 = 5
  Profile = -> Pad029 [Face78]
  Refine = true
  Suppressed = false
  Type = 0
FEATURE [PartDesign::Pocket] Pocket025
  BaseFeature = -> Pocket024
  Direction = (0,-1,0)
  Length = 1
  Length2 = 5
  Profile = -> Pocket024 [Face8]
  Refine = true
  Suppressed = false
  Type = 0
FEATURE [PartDesign::Fillet] Fillet002
  Base = -> Pocket025 [Edge7,Edge59,Edge9,Edge65]
  BaseFeature = -> Pocket025
  Radius = 0.5
  Refine = true
  SupportTransform = false
  Suppressed = false
  UseAllEdges = false
FEATURE [Sketcher::SketchObject] Sketch051
  ArcFitTolerance = 1e-06
  AttachmentSupport = -> [Fillet002]
  ExternalGeometry = -> [Fillet002]
  FullyConstrained = true
  MakeInternals = false
  MapMode = 5
  Placement = pos=(0,12.05,0) rot=(0,0.707107,0.707107;3.14159rad)
  sketch-geometry (4):
    g0: ArcOfCircle CenterX=8.1 CenterY=-2 CenterZ=0 NormalX=0 NormalY=0 NormalZ=1 AngleXU=0 Radius=5.5 StartAngle=3.14159 EndAngle=6.28319
    g1: LineSegment StartX=13.6 StartY=-2 StartZ=0 EndX=13.6 EndY=0 EndZ=0
    g2: LineSegment StartX=2.6 StartY=-2 StartZ=0 EndX=2.6 EndY=0 EndZ=0
    g3: LineSegment StartX=2.6 StartY=0 StartZ=0 EndX=13.6 EndY=0 EndZ=0
  constraints (13):
    c: Diameter(g0) = 11
    c: Tangent(g0,g-3)
    c: DistanceY(g0,g0) = 0
    c: DistanceY(g0,g0) = 0
    c: Coincident(g1,g0)
    c: PointOnObject(g1,g-4)
    c: Vertical(g1)
    c: Coincident(g2,g0)
    c: PointOnObject(g2,g-4)
    c: Vertical(g2)
    c: Coincident(g3,g2)
    c: Coincident(g3,g1)
    c: DistanceX(g-1,g2) = 2.6
FEATURE [PartDesign::Pad] Pad030
  BaseFeature = -> Fillet002
  Direction = (0,1,-2e-16)
  Length = 1
  Length2 = 10
  Profile = -> Sketch051
  ReferenceAxis = -> Sketch051 [N_Axis]
  Refine = true
  Suppressed = false
  Type = 0
FEATURE [Sketcher::SketchObject] Sketch052
  ArcFitTolerance = 1e-06
  AttachmentSupport = -> [Pad030]
  ExternalGeometry = -> [Pad030]
  FullyConstrained = true
  MakeInternals = false
  MapMode = 5
  Placement = pos=(0,-12.05,0) rot=(1,0,0;1.5708rad)
  sketch-geometry (4):
    g0: ArcOfCircle CenterX=-8.1 CenterY=-2 CenterZ=0 NormalX=0 NormalY=0 NormalZ=1 AngleXU=0 Radius=5.5 StartAngle=3.14159 EndAngle=6.28319
    g1: LineSegment StartX=-2.6 StartY=-2 StartZ=0 EndX=-2.6 EndY=0 EndZ=0
    g2: LineSegment StartX=-13.6 StartY=-2 StartZ=0 EndX=-13.6 EndY=0 EndZ=0
    g3: LineSegment StartX=-13.6 StartY=0 StartZ=0 EndX=-2.6 EndY=0 EndZ=0
  constraints (13):
    c: Diameter(g0) = 11
    c: Tangent(g0,g-4)
    c: DistanceY(g0,g0) = 0
    c: DistanceY(g0,g0) = 0
    c: Coincident(g1,g0)
    c: PointOnObject(g1,g-3)
    c: Vertical(g1)
    c: Coincident(g2,g0)
    c: PointOnObject(g2,g-3)
    c: Vertical(g2)
    c: Coincident(g3,g2)
    c: Coincident(g3,g1)
    c: DistanceX(g1,g-1) = 2.6
FEATURE [PartDesign::Pad] Pad031
  BaseFeature = -> Pad030
  Direction = (0,-1,2e-16)
  Length = 1
  Length2 = 10
  Profile = -> Sketch052
  ReferenceAxis = -> Sketch052 [N_Axis]
  Refine = true
  Suppressed = false
  Type = 0
FEATURE [Sketcher::SketchObject] Sketch053
  ArcFitTolerance = 1e-06
  AttachmentSupport = -> [Pad031]
  ExternalGeometry = -> [Pad031]
  FullyConstrained = true
  MakeInternals = false
  MapMode = 5
  Placement = pos=(0,-13.05,3.5e-15) rot=(1,0,0;1.5708rad)
  sketch-geometry (4):
    g0: ArcOfCircle CenterX=-8.1 CenterY=-2 CenterZ=0 NormalX=0 NormalY=0 NormalZ=1 AngleXU=0 Radius=2.25 StartAngle=3.14159 EndAngle=6.28319
    g1: LineSegment StartX=-10.35 StartY=-2 StartZ=0 EndX=-10.35 EndY=0 EndZ=0
    g2: LineSegment StartX=-5.85 StartY=-2 StartZ=0 EndX=-5.85 EndY=-3.3e-15 EndZ=0
    g3: LineSegment StartX=-5.85 StartY=-3.3e-15 StartZ=0 EndX=-10.35 EndY=0 EndZ=0
  constraints (13):
    c: Diameter(g0) = 4.5
    c: Coincident(g0,g-3)
    c: DistanceY(g0,g-4) = 2
    c: DistanceY(g0,g0) = 0
    c: DistanceY(g0,g0) = 0
    c: Coincident(g1,g0)
    c: PointOnObject(g1,g-4)
    c: Vertical(g1)
    c: Coincident(g2,g0)
    c: PointOnObject(g2,g-4)
    c: Vertical(g2)
    c: Coincident(g3,g2)
    c: Coincident(g3,g1)
FEATURE [PartDesign::Pocket] Pocket026
  BaseFeature = -> Pad031
  Direction = (0,1,-2e-16)
  Length = 3
  Length2 = 5
  Profile = -> Sketch053
  ReferenceAxis = -> Sketch053 [N_Axis]
  Refine = true
  Suppressed = false
  Type = 0
FEATURE [Sketcher::SketchObject] Sketch054
  ArcFitTolerance = 1e-06
  AttachmentSupport = -> [Pocket026]
  ExternalGeometry = -> [Pocket026]
  FullyConstrained = true
  MakeInternals = false
  MapMode = 5
  Placement = pos=(0,13.05,-3.5e-15) rot=(0,0.707107,0.707107;3.14159rad)
  sketch-geometry (4):
    g0: ArcOfCircle CenterX=8.1 CenterY=-2 CenterZ=0 NormalX=0 NormalY=0 NormalZ=1 AngleXU=0 Radius=2.25 StartAngle=3.14159 EndAngle=6.28319
    g1: LineSegment StartX=5.85 StartY=-2 StartZ=0 EndX=5.85 EndY=3.3e-15 EndZ=0
    g2: LineSegment StartX=10.35 StartY=-2 StartZ=0 EndX=10.35 EndY=3.3e-15 EndZ=0
    g3: LineSegment StartX=10.35 StartY=3.4e-15 StartZ=0 EndX=5.85 EndY=3.4e-15 EndZ=0
  constraints (12):
    c: Coincident(g0,g-4)
    c: DistanceY(g0,g0) = 0
    c: DistanceY(g0,g0) = 0
    c: Coincident(g1,g0)
    c: PointOnObject(g1,g-3)
    c: Vertical(g1)
    c: Coincident(g2,g0)
    c: PointOnObject(g2,g-3)
    c: Vertical(g2)
    c: Coincident(g3,g2)
    c: Coincident(g3,g1)
    c: Diameter(g0) = 4.5
FEATURE [PartDesign::Pocket] Pocket027
  BaseFeature = -> Pocket026
  Direction = (0,-1,2e-16)
  Length = 3
  Length2 = 5
  Profile = -> Sketch054
  ReferenceAxis = -> Sketch054 [N_Axis]
  Refine = true
  Suppressed = false
  Type = 0
FEATURE [Sketcher::SketchObject] Sketch055
  ArcFitTolerance = 1e-06
  AttachmentSupport = -> [Pocket027]
  ExternalGeometry = -> [Pocket027]
  FullyConstrained = true
  MakeInternals = false
  MapMode = 5
  Placement = pos=(0,0,-6) rot=(0,0,1;0rad)
  sketch-geometry (16):
    g0: ArcOfCircle CenterX=-18 CenterY=-8.55 CenterZ=0 NormalX=0 NormalY=0 NormalZ=1 AngleXU=0 Radius=1 StartAngle=-9e-16 EndAngle=1.5708
    g1: LineSegment StartX=-17 StartY=-8.55 StartZ=0 EndX=-17 EndY=-3.5 EndZ=0
    g2: LineSegment StartX=-25.6 StartY=-8.55 StartZ=0 EndX=-25.6 EndY=-3.5 EndZ=0
    g3: ArcOfCircle CenterX=-24.6 CenterY=-3.5 CenterZ=0 NormalX=0 NormalY=0 NormalZ=1 AngleXU=0 Radius=1 StartAngle=1.5708 EndAngle=3.14159
    g4: ArcOfCircle CenterX=-18 CenterY=-3.5 CenterZ=0 NormalX=0 NormalY=0 NormalZ=1 AngleXU=0 Radius=1 StartAngle=0 EndAngle=1.5708
    g5: LineSegment StartX=-18 StartY=-2.5 StartZ=0 EndX=-24.6 EndY=-2.5 EndZ=0
    g6: LineSegment StartX=-18 StartY=-7.55 StartZ=0 EndX=-24.6 EndY=-7.55 EndZ=0
    g7: ArcOfCircle CenterX=-24.6 CenterY=-8.54999 CenterZ=0 NormalX=0 NormalY=0 NormalZ=1 AngleXU=0 Radius=0.999994 StartAngle=1.57079 EndAngle=3.1416
    g8: LineSegment StartX=-24.6 StartY=2.5 StartZ=0 EndX=-18 EndY=2.5 EndZ=0
    g9: LineSegment StartX=-24.6 StartY=7.55 StartZ=0 EndX=-18 EndY=7.55 EndZ=0
    g10: ArcOfCircle CenterX=-18 CenterY=8.55 CenterZ=0 NormalX=0 NormalY=0 NormalZ=1 AngleXU=0 Radius=1 StartAngle=4.71239 EndAngle=6.28319
    g11: LineSegment StartX=-25.6 StartY=8.55 StartZ=0 EndX=-25.6 EndY=3.5 EndZ=0
    g12: LineSegment StartX=-17 StartY=8.55 StartZ=0 EndX=-17 EndY=3.5 EndZ=0
    g13: ArcOfCircle CenterX=-24.6 CenterY=3.5 CenterZ=0 NormalX=0 NormalY=0 NormalZ=1 AngleXU=0 Radius=1 StartAngle=3.14159 EndAngle=4.71239
    g14: ArcOfCircle CenterX=-18 CenterY=3.5 CenterZ=0 NormalX=0 NormalY=0 NormalZ=1 AngleXU=0 Radius=1 StartAngle=4.71239 EndAngle=6.28319
    g15: ArcOfCircle CenterX=-24.6 CenterY=8.55 CenterZ=0 NormalX=0 NormalY=0 NormalZ=1 AngleXU=0 Radius=1 StartAngle=3.14159 EndAngle=4.71239
  constraints (45):
    c: Tangent(g0,g-4) = -1.5708
    c: Coincident(g0,g-4)
    c: Vertical(g1)
    c: Vertical(g2)
    c: Coincident(g3,g2)
    c: Coincident(g4,g1)
    c: PointOnObject(g4,g-5)
    c: Coincident(g5,g4)
    c: Horizontal(g5)
    c: Radius(g3) = 1
    c: Radius(g4) = 1
    c: DistanceY(g1,g4) = 0
    c: DistanceY(g2,g3) = 0
    c: Coincident(g5,g3)
    c: DistanceX(g3,g3) = 0
    c: DistanceX(g4,g4) = 0
    c: Coincident(g2,g-3)
    c: Coincident(g1,g0)
    c: Coincident(g6,g0)
    c: Coincident(g6,g-3)
    c: Coincident(g7,g6)
    c: Coincident(g7,g2)
    c: Tangent(g7,g-3)
    c: PointOnObject(g8,g-9)
    c: PointOnObject(g8,g-8)
    c: Coincident(g9,g-7)
    c: Coincident(g10,g9)
    c: Vertical(g11)
    c: Coincident(g12,g10)
    c: Vertical(g12)
    c: Coincident(g13,g8)
    c: Coincident(g13,g11)
    c: Coincident(g14,g12)
    c: Coincident(g14,g8)
    c: DistanceY(g14,g12) = 0
    c: DistanceY(g13,g11) = 0
    c: DistanceX(g13,g8) = 0
    c: DistanceX(g14,g8) = 0
    c: Radius(g13) = 1
    c: Radius(g14) = 1
    c: Tangent(g10,g-7) = -1.5708
    c: Coincident(g15,g-10)
    c: Tangent(g15,g-10) = -1.5708
    c: Coincident(g11,g15)
    c: Coincident(g9,g15)
FEATURE [PartDesign::Pad] Pad032
  BaseFeature = -> Pocket027
  Direction = (0,0,1)
  Length = 1
  Length2 = 10
  Profile = -> Sketch055
  ReferenceAxis = -> Sketch055 [N_Axis]
  Refine = true
  Suppressed = false
  Type = 0
FEATURE [Sketcher::SketchObject] Sketch056
  ArcFitTolerance = 1e-06
  AttachmentSupport = -> [Pad032]
  ExternalGeometry = -> [Pad032]
  FullyConstrained = true
  MakeInternals = false
  MapMode = 5
  Placement = pos=(0,0,-7.5) rot=(1,0,0;3.14159rad)
  sketch-geometry (4):
    g0: LineSegment StartX=-35.5518 StartY=4 StartZ=0 EndX=-35.5518 EndY=-4 EndZ=0
    g1: LineSegment StartX=-35.5518 StartY=-4 StartZ=0 EndX=-24.1 EndY=-4 EndZ=0
    g2: LineSegment StartX=-24.1 StartY=-4 StartZ=0 EndX=-24.1 EndY=4 EndZ=0
    g3: LineSegment StartX=-24.1 StartY=4 StartZ=0 EndX=-35.5518 EndY=4 EndZ=0
  constraints (10):
    c: Coincident(g0,g1)
    c: Coincident(g1,g2)
    c: Coincident(g2,g3)
    c: Coincident(g3,g0)
    c: Vertical(g2)
    c: Horizontal(g1)
    c: Horizontal(g3)
    c: Coincident(g0,g-3)
    c: PointOnObject(g1,g-5)
    c: Coincident(g0,g-3)
FEATURE [PartDesign::Pad] Pad033
  BaseFeature = -> Pad032
  Direction = (0,0,-1)
  Length = 1.5
  Length2 = 10
  Profile = -> Sketch056
  ReferenceAxis = -> Sketch056 [N_Axis]
  Refine = true
  Suppressed = false
  Type = 0
FEATURE [Sketcher::SketchObject] Sketch057
  ArcFitTolerance = 1e-06
  AttachmentSupport = -> [Pad033]
  ExternalGeometry = -> [Pad033]
  FullyConstrained = true
  MakeInternals = false
  MapMode = 5
  Placement = pos=(0,4,0) rot=(0,0.707107,0.707107;3.14159rad)
  sketch-geometry (3):
    g0: LineSegment StartX=35.5518 StartY=-7.5 StartZ=0 EndX=35.5518 EndY=-9 EndZ=0
    g1: LineSegment StartX=35.5518 StartY=-9 StartZ=0 EndX=34.0518 EndY=-9 EndZ=0
    g2: LineSegment StartX=35.5518 StartY=-7.5 StartZ=0 EndX=34.0518 EndY=-9 EndZ=0
  constraints (7):
    c: Coincident(g0,g-3)
    c: Coincident(g0,g-4)
    c: Coincident(g1,g0)
    c: PointOnObject(g1,g-4)
    c: Coincident(g2,g0)
    c: Coincident(g2,g1)
    c: Angle(g2,g0) = 0.785398
FEATURE [PartDesign::Pocket] Pocket028
  BaseFeature = -> Pad033
  Direction = (0,-1,2e-16)
  Length = 8
  Length2 = 5
  Profile = -> Sketch057
  ReferenceAxis = -> Sketch057 [N_Axis]
  Refine = true
  Suppressed = false
  Type = 0
FEATURE [Sketcher::SketchObject] Sketch058
  ArcFitTolerance = 1e-06
  AttachmentSupport = -> [Pocket028]
  ExternalGeometry = -> [Pocket028]
  FullyConstrained = true
  MakeInternals = false
  MapMode = 5
  Placement = pos=(0,0,-6) rot=(1,0,0;3.14159rad)
  sketch-geometry (8):
    g0: LineSegment StartX=-24.1 StartY=-2.5 StartZ=0 EndX=-24.1 EndY=-4 EndZ=0
    g1: LineSegment StartX=-24.1 StartY=-4 StartZ=0 EndX=-18.5 EndY=-4 EndZ=0
    g2: LineSegment StartX=-18.5 StartY=-4 StartZ=0 EndX=-18.5 EndY=-2.5 EndZ=0
    g3: LineSegment StartX=-18.5 StartY=-2.5 StartZ=0 EndX=-24.1 EndY=-2.5 EndZ=0
    g4: LineSegment StartX=-24.1 StartY=2.5 StartZ=0 EndX=-18.5 EndY=2.5 EndZ=0
    g5: LineSegment StartX=-18.5 StartY=2.5 StartZ=0 EndX=-18.5 EndY=4 EndZ=0
    g6: LineSegment StartX=-18.5 StartY=4 StartZ=0 EndX=-24.1 EndY=4 EndZ=0
    g7: LineSegment StartX=-24.1 StartY=4 StartZ=0 EndX=-24.1 EndY=2.5 EndZ=0
  constraints (22):
    c: Coincident(g0,g1)
    c: Coincident(g1,g2)
    c: Coincident(g2,g3)
    c: Coincident(g3,g0)
    c: Vertical(g0)
    c: Vertical(g2)
    c: Horizontal(g1)
    c: Horizontal(g3)
    c: Coincident(g0,g-8)
    c: PointOnObject(g1,g-6)
    c: Coincident(g4,g5)
    c: Coincident(g5,g6)
    c: Coincident(g6,g7)
    c: Coincident(g7,g4)
    c: Horizontal(g4)
    c: Horizontal(g6)
    c: Vertical(g5)
    c: Vertical(g7)
    c: Coincident(g4,g-4)
    c: PointOnObject(g5,g-5)
    c: DistanceY(g5,g5) = 1.5
    c: DistanceY(g2,g2) = 1.5
FEATURE [PartDesign::Pad] Pad034
  BaseFeature = -> Pocket028
  Direction = (0,0,-1)
  Length = 1.5
  Length2 = 10
  Profile = -> Sketch058
  ReferenceAxis = -> Sketch058 [N_Axis]
  Refine = true
  Suppressed = false
  Type = 0
FEATURE [Sketcher::SketchObject] Sketch059
  ArcFitTolerance = 1e-06
  AttachmentSupport = -> [Pad034]
  ExternalGeometry = -> [Pad034]
  FullyConstrained = true
  MakeInternals = false
  MapMode = 5
  Placement = pos=(0,0,-7.5) rot=(1,0,0;3.14159rad)
  sketch-geometry (8):
    g0: LineSegment StartX=-24.1 StartY=4 StartZ=0 EndX=-24.1 EndY=2.5 EndZ=0
    g1: LineSegment StartX=-24.1 StartY=2.5 StartZ=0 EndX=-4.938e-13 EndY=2.5 EndZ=0
    g2: LineSegment StartX=-4.938e-13 StartY=2.5 StartZ=0 EndX=-4.938e-13 EndY=4 EndZ=0
    g3: LineSegment StartX=-4.938e-13 StartY=4 StartZ=0 EndX=-24.1 EndY=4 EndZ=0
    g4: LineSegment StartX=-24.1 StartY=-2.5 StartZ=0 EndX=-24.1 EndY=-4 EndZ=0
    g5: LineSegment StartX=-24.1 StartY=-4 StartZ=0 EndX=-7.994e-13 EndY=-4 EndZ=0
    g6: LineSegment StartX=-7.994e-13 StartY=-4 StartZ=0 EndX=-7.994e-13 EndY=-2.5 EndZ=0
    g7: LineSegment StartX=-7.994e-13 StartY=-2.5 StartZ=0 EndX=-24.1 EndY=-2.5 EndZ=0
  constraints (22):
    c: Coincident(g0,g1)
    c: Coincident(g1,g2)
    c: Coincident(g2,g3)
    c: Coincident(g3,g0)
    c: Vertical(g0)
    c: Vertical(g2)
    c: Horizontal(g1)
    c: Horizontal(g3)
    c: Coincident(g0,g-4)
    c: PointOnObject(g1,g-7)
    c: Coincident(g4,g5)
    c: Coincident(g5,g6)
    c: Coincident(g6,g7)
    c: Coincident(g7,g4)
    c: Vertical(g4)
    c: Vertical(g6)
    c: Horizontal(g5)
    c: Horizontal(g7)
    c: Coincident(g4,g-6)
    c: PointOnObject(g5,g-7)
    c: PointOnObject(g-5,g5)
    c: PointOnObject(g-3,g1)
FEATURE [PartDesign::Pad] Pad035
  BaseFeature = -> Pad034
  Direction = (0,0,-1)
  Length = 4
  Length2 = 10
  Profile = -> Sketch059
  ReferenceAxis = -> Sketch059 [N_Axis]
  Refine = true
  Suppressed = false
  Type = 0
FEATURE [Sketcher::SketchObject] Sketch060
  ArcFitTolerance = 1e-06
  AttachmentSupport = -> [Pad035]
  ExternalGeometry = -> [Pad035]
  FullyConstrained = true
  MakeInternals = false
  MapMode = 5
  Placement = pos=(0,4,0) rot=(0,0.707107,0.707107;3.14159rad)
  sketch-geometry (6):
    g0: LineSegment StartX=7.994e-13 StartY=-8.5 StartZ=0 EndX=7.994e-13 EndY=-11.5 EndZ=0
    g1: LineSegment StartX=7.994e-13 StartY=-11.5 StartZ=0 EndX=6 EndY=-11.5 EndZ=0
    g2: LineSegment StartX=6 StartY=-11.5 StartZ=0 EndX=7.994e-13 EndY=-8.5 EndZ=0
    g3: LineSegment StartX=24.1 StartY=-9 StartZ=0 EndX=19.7699 EndY=-11.5 EndZ=0
    g4: LineSegment StartX=19.7699 StartY=-11.5 StartZ=0 EndX=24.1 EndY=-11.5 EndZ=0
    g5: LineSegment StartX=24.1 StartY=-11.5 StartZ=0 EndX=24.1 EndY=-9 EndZ=0
  constraints (15):
    c: PointOnObject(g0,g-5)
    c: Coincident(g0,g-5)
    c: Coincident(g1,g0)
    c: PointOnObject(g1,g-4)
    c: Coincident(g2,g1)
    c: Coincident(g2,g0)
    c: Coincident(g3,g-3)
    c: PointOnObject(g3,g-4)
    c: Coincident(g4,g3)
    c: Coincident(g4,g-4)
    c: Coincident(g5,g4)
    c: Coincident(g5,g3)
    c: Angle(g3,g5) = 1.0472
    c: DistanceY(g0,g-5) = 1
    c: DistanceX(g1,g1) = 6
FEATURE [PartDesign::Pocket] Pocket029
  BaseFeature = -> Pad035
  Direction = (0,-1,2e-16)
  Length = 8
  Length2 = 5
  Profile = -> Sketch060
  ReferenceAxis = -> Sketch060 [N_Axis]
  Refine = true
  Suppressed = false
  Type = 0
FEATURE [Sketcher::SketchObject] Sketch061
  ArcFitTolerance = 1e-06
  AttachmentSupport = -> [Pocket029]
  ExternalGeometry = -> [Pocket029]
  FullyConstrained = true
  MakeInternals = false
  MapMode = 5
  Placement = pos=(0,-2.5,0) rot=(0,0.707107,0.707107;3.14159rad)
  sketch-geometry (9):
    g0: LineSegment StartX=4.938e-13 StartY=-7.5 StartZ=0 EndX=0 EndY=-8.5 EndZ=0
    g1: LineSegment StartX=7.976e-13 StartY=-8.5 StartZ=0 EndX=6 EndY=-11.5 EndZ=0
    g2: LineSegment StartX=6 StartY=-11.5 StartZ=0 EndX=19.7699 EndY=-11.5 EndZ=0
    g3: LineSegment StartX=19.7699 StartY=-11.5 StartZ=0 EndX=24.1 EndY=-9 EndZ=0
    g4: LineSegment StartX=24.1 StartY=-9 StartZ=0 EndX=24.1 EndY=-7.5 EndZ=0
    g5: LineSegment StartX=24.1 StartY=-7.5 StartZ=0 EndX=19.7699 EndY=-10 EndZ=0
    g6: LineSegment StartX=19.7699 StartY=-10 StartZ=0 EndX=6.5 EndY=-10 EndZ=0
    g7: LineSegment StartX=4.938e-13 StartY=-7.5 StartZ=0 EndX=1.5 EndY=-7.5 EndZ=0
    g8: LineSegment StartX=6.5 StartY=-10 StartZ=0 EndX=1.5 EndY=-7.5 EndZ=0
  constraints (20):
    c: Coincident(g0,g-8)
    c: Coincident(g0,g-3)
    c: Coincident(g1,g-3)
    c: Coincident(g1,g-4)
    c: Coincident(g2,g1)
    c: Coincident(g2,g-5)
    c: Coincident(g3,g2)
    c: Coincident(g3,g-6)
    c: Coincident(g4,g3)
    c: Coincident(g4,g-6)
    c: Coincident(g5,g4)
    c: Coincident(g6,g5)
    c: Horizontal(g6)
    c: Coincident(g7,g0)
    c: Coincident(g7,g-9)
    c: Coincident(g8,g6)
    c: Coincident(g8,g7)
    c: Parallel(g8,g1)
    c: Parallel(g5,g3)
    c: DistanceY(g2,g5) = 1.5
FEATURE [PartDesign::Pad] Pad036
  BaseFeature = -> Pocket029
  Direction = (0,1,-2e-16)
  Length = 5
  Length2 = 10
  Profile = -> Sketch061
  ReferenceAxis = -> Sketch061 [N_Axis]
  Refine = true
  Suppressed = false
  Type = 0
FEATURE [Sketcher::SketchObject] Sketch062
  ArcFitTolerance = 1e-06
  AttachmentSupport = -> [Pad036]
  ExternalGeometry = -> [Pad036]
  FullyConstrained = true
  MakeInternals = false
  MapMode = 5
  Placement = pos=(0,0,-7.5) rot=(1,0,0;3.14159rad)
  sketch-geometry (12):
    g0: LineSegment StartX=-1 StartY=-4 StartZ=0 EndX=-1 EndY=-10.05 EndZ=0
    g1: ArcOfCircle CenterX=-2 CenterY=-10.05 CenterZ=0 NormalX=0 NormalY=0 NormalZ=1 AngleXU=0 Radius=1 StartAngle=4.71239 EndAngle=6.28319
    g2: LineSegment StartX=-2 StartY=-11.05 StartZ=0 EndX=-9.9 EndY=-11.05 EndZ=0
    g3: ArcOfCircle CenterX=-9.9 CenterY=-10.05 CenterZ=0 NormalX=0 NormalY=0 NormalZ=1 AngleXU=0 Radius=1 StartAngle=3.14159 EndAngle=4.71239
    g4: LineSegment StartX=-10.9 StartY=-10.05 StartZ=0 EndX=-10.9 EndY=-4 EndZ=0
    g5: LineSegment StartX=-10.9 StartY=-4 StartZ=0 EndX=-1 EndY=-4 EndZ=0
    g6: LineSegment StartX=-1 StartY=4 StartZ=0 EndX=-1 EndY=10.05 EndZ=0
    g7: ArcOfCircle CenterX=-2 CenterY=10.05 CenterZ=0 NormalX=0 NormalY=0 NormalZ=1 AngleXU=0 Radius=1 StartAngle=2e-16 EndAngle=1.5708
    g8: LineSegment StartX=-2 StartY=11.05 StartZ=0 EndX=-9.9 EndY=11.05 EndZ=0
    g9: ArcOfCircle CenterX=-9.9 CenterY=10.05 CenterZ=0 NormalX=0 NormalY=0 NormalZ=1 AngleXU=0 Radius=1 StartAngle=1.5708 EndAngle=3.14159
    g10: LineSegment StartX=-10.9 StartY=10.05 StartZ=0 EndX=-10.9 EndY=4 EndZ=0
    g11: LineSegment StartX=-10.9 StartY=4 StartZ=0 EndX=-1 EndY=4 EndZ=0
  constraints (40):
    c: PointOnObject(g0,g-8)
    c: Vertical(g0)
    c: Coincident(g1,g0)
    c: Coincident(g2,g1)
    c: Horizontal(g2)
    c: Coincident(g3,g2)
    c: Coincident(g4,g3)
    c: PointOnObject(g4,g-8)
    c: Coincident(g5,g4)
    c: DistanceX(g2,g3) = 0
    c: DistanceX(g1,g1) = 0
    c: Radius(g3) = 1
    c: Radius(g1) = 1
    c: DistanceY(g1,g0) = 0
    c: DistanceY(g3,g3) = 0
    c: Vertical(g4)
    c: DistanceX(g3,g0) = 9.9
    c: DistanceX(g0,g-6) = 1
    c: DistanceY(g-7,g1) = 1
    c: Coincident(g5,g0)
    c: PointOnObject(g6,g-3)
    c: Vertical(g6)
    c: Coincident(g7,g6)
    c: Coincident(g8,g7)
    c: Horizontal(g8)
    c: Coincident(g9,g8)
    c: Coincident(g10,g9)
    c: PointOnObject(g10,g-3)
    c: Vertical(g10)
    c: Coincident(g11,g10)
    c: Coincident(g11,g6)
    c: Radius(g9) = 1
    c: Radius(g7) = 1
    c: DistanceX(g9,g8) = 0
    c: DistanceX(g7,g7) = 0
    c: DistanceY(g7,g6) = 0
    c: DistanceX(g6,g-4) = 1
    c: DistanceY(g7,g-5) = 1
    c: DistanceX(g10,g6) = 9.9
    c: DistanceY(g9,g9) = 0
FEATURE [PartDesign::Pad] Pad037
  BaseFeature = -> Pad036
  Direction = (0,0,-1)
  Length = 1
  Length2 = 10
  Profile = -> Sketch062
  ReferenceAxis = -> Sketch062 [N_Axis]
  Refine = true
  Suppressed = false
  Type = 0
FEATURE [Sketcher::SketchObject] Sketch063
  ArcFitTolerance = 1e-06
  AttachmentSupport = -> [Pad037]
  ExternalGeometry = -> [Pad037]
  FullyConstrained = true
  MakeInternals = false
  MapMode = 5
  Placement = pos=(0,0,-6) rot=(0,0,1;0rad)
  sketch-geometry (10):
    g0: LineSegment StartX=-9.9 StartY=10.55 StartZ=0 EndX=-9.9 EndY=5.2 EndZ=0
    g1: LineSegment StartX=-9.9 StartY=5.2 StartZ=0 EndX=-3 EndY=5.2 EndZ=0
    g2: LineSegment StartX=-3 StartY=5.2 StartZ=0 EndX=-3 EndY=9.22712 EndZ=0
    g3: LineSegment StartX=-9.9 StartY=10.55 StartZ=0 EndX=-3.5 EndY=10.55 EndZ=0
    g4: ArcOfCircle CenterX=-1.50002 CenterY=10.55 CenterZ=0 NormalX=0 NormalY=0 NormalZ=1 AngleXU=0 Radius=1.99998 StartAngle=3.14159 EndAngle=3.86433
    g5: LineSegment StartX=-3 StartY=-5.2 StartZ=0 EndX=-9.9 EndY=-5.2 EndZ=0
    g6: LineSegment StartX=-9.9 StartY=-5.2 StartZ=0 EndX=-9.9 EndY=-10.55 EndZ=0
    g7: LineSegment StartX=-3 StartY=-5.2 StartZ=0 EndX=-3 EndY=-9.22712 EndZ=0
    g8: ArcOfCircle CenterX=-1.50001 CenterY=-10.55 CenterZ=0 NormalX=0 NormalY=0 NormalZ=1 AngleXU=0 Radius=1.99999 StartAngle=2.41886 EndAngle=3.1416
    g9: LineSegment StartX=-3.5 StartY=-10.55 StartZ=0 EndX=-9.9 EndY=-10.55 EndZ=0
  constraints (30):
    c: PointOnObject(g0,g-5)
    c: PointOnObject(g0,g-4)
    c: Vertical(g0)
    c: Coincident(g1,g0)
    c: PointOnObject(g1,g-4)
    c: Coincident(g2,g1)
    c: PointOnObject(g2,g-3)
    c: Vertical(g2)
    c: Coincident(g3,g0)
    c: Coincident(g3,g-5)
    c: Coincident(g4,g3)
    c: Coincident(g4,g2)
    c: Tangent(g4,g-3)
    c: DistanceX(g2,g-6) = 1.5
    c: DistanceX(g0,g2) = 6.9
    c: PointOnObject(g5,g-8)
    c: PointOnObject(g5,g-8)
    c: Coincident(g6,g5)
    c: PointOnObject(g6,g-10)
    c: Vertical(g6)
    c: Coincident(g7,g5)
    c: PointOnObject(g7,g-9)
    c: Vertical(g7)
    c: Coincident(g8,g7)
    c: Coincident(g8,g-10)
    c: Coincident(g9,g8)
    c: Coincident(g9,g6)
    c: DistanceX(g5,g-8) = 1.5
    c: DistanceX(g5,g5) = 6.9
    c: Tangent(g8,g-9)
FEATURE [PartDesign::Body] Body001  label="Front_Torso"
  AllowCompound = false
  Group = -> [Binder,Pad025,Sketch044,Pad026,Sketch045,Pocket021,Sketch046,Pad027,Sketch047,Pad028,Sketch048,Pocket022,Sketch049,Pocket023,Sketch050,Pad029,Pocket024,Pocket025,Fillet002,Sketch051,Pad030,Sketch052,Pad031,Sketch053,Pocket026,Sketch054,Pocket027,Sketch055,Pad032,Sketch056,Pad033,Sketch057,Pocket028,Sketch058,Pad034,Sketch059,Pad035,Sketch060,Pocket029,Sketch061,Pad036,Sketch062,Pad037,Sketch063,+36 more]
  Origin = -> Origin001
  Tip = -> Pad235
COMPONENT P2 — recipe-attached ("Legs", modeled in this document).
Construction recipe (the document's own serialized feature program — sketch geometry with constraints, then the solid features built on it; lengths are millimeters unless a unit is written):

FEATURE [PartDesign::SubShapeBinder] Binder001
  BindCopyOnChange = 0
  BindMode = 2
  ClaimChildren = false
  Context = -> Body003 [Binder001.]
  Fuse = false
  MakeFace = true
  OffsetFill = false
  OffsetIntersection = false
  OffsetJoinType = 0
  OffsetOpenResult = false
  PartialLoad = false
  Refine = true
  Relative = true
  _Version = 2
FEATURE [Sketcher::SketchObject] Sketch097
  ArcFitTolerance = 1e-06
  AttachmentSupport = -> [Binder001]
  ExternalGeometry = -> [Binder001]
  FullyConstrained = true
  MakeInternals = false
  MapMode = 5
  Placement = pos=(0,0,2.5) rot=(1,0,0;3.14159rad)
  sketch-geometry (5):
    g0: LineSegment StartX=-26.8 StartY=3.1 StartZ=0 EndX=-33.8 EndY=3.1 EndZ=0
    g1: LineSegment StartX=-33.8 StartY=3.1 StartZ=0 EndX=-33.8 EndY=-3.1 EndZ=0
    g2: LineSegment StartX=-33.8 StartY=-3.1 StartZ=0 EndX=-26.8 EndY=-3.1 EndZ=0
    g3: LineSegment StartX=-26.8 StartY=-3.1 StartZ=0 EndX=-26.8 EndY=3.1 EndZ=0
    g4: Circle CenterX=-30.45 CenterY=0 CenterZ=0 NormalX=0 NormalY=0 NormalZ=1 AngleXU=0 Radius=1.15
  constraints (15):
    c: Coincident(g0,g1)
    c: Coincident(g1,g2)
    c: Coincident(g2,g3)
    c: Coincident(g3,g0)
    c: Horizontal(g0)
    c: Horizontal(g2)
    c: Vertical(g1)
    c: Vertical(g3)
    c: DistanceY(g3,g3) = 6.2
    c: DistanceY(g-1,g0) = 3.1
    c: DistanceX(g0,g0) = 7
    c: DistanceX(g2,g-1) = 26.8
    c: Coincident(g4,g-3)
    c: Equal(g4,g-3)
    c: DistanceX(g0,g4) = 3.35
FEATURE [PartDesign::Pad] Pad059
  Direction = (0,0,-1)
  Length = 2.5
  Length2 = 10
  Profile = -> Sketch097
  ReferenceAxis = -> Sketch097 [N_Axis]
  Refine = true
  Suppressed = false
  Type = 0
FEATURE [Sketcher::SketchObject] Sketch098
  ArcFitTolerance = 1e-06
  AttachmentSupport = -> [Pad059]
  ExternalGeometry = -> [Pad059]
  FullyConstrained = true
  MakeInternals = false
  MapMode = 5
  Placement = pos=(0,0,9e-16) rot=(1,0,0;3.14159rad)
  sketch-geometry (8):
    g0: LineSegment StartX=-26.8 StartY=-3.1 StartZ=0 EndX=-34.8 EndY=-3.1 EndZ=0
    g1: LineSegment StartX=-34.8 StartY=-3.1 StartZ=0 EndX=-34.8 EndY=-8.8 EndZ=0
    g2: LineSegment StartX=-34.8 StartY=-8.8 StartZ=0 EndX=-26.8 EndY=-8.8 EndZ=0
    g3: LineSegment StartX=-26.8 StartY=-8.8 StartZ=0 EndX=-26.8 EndY=-3.1 EndZ=0
    g4: LineSegment StartX=-26.8 StartY=3.1 StartZ=0 EndX=-26.8 EndY=8.8 EndZ=0
    g5: LineSegment StartX=-26.8 StartY=8.8 StartZ=0 EndX=-34.8 EndY=8.8 EndZ=0
    g6: LineSegment StartX=-34.8 StartY=8.8 StartZ=0 EndX=-34.8 EndY=3.1 EndZ=0
    g7: LineSegment StartX=-34.8 StartY=3.1 StartZ=0 EndX=-26.8 EndY=3.1 EndZ=0
  constraints (22):
    c: Coincident(g0,g1)
    c: Coincident(g1,g2)
    c: Coincident(g2,g3)
    c: Coincident(g3,g0)
    c: Horizontal(g0)
    c: Horizontal(g2)
    c: Vertical(g1)
    c: Vertical(g3)
    c: Coincident(g0,g-5)
    c: Coincident(g4,g5)
    c: Coincident(g5,g6)
    c: Coincident(g6,g7)
    c: Coincident(g7,g4)
    c: Vertical(g4)
    c: Vertical(g6)
    c: Horizontal(g5)
    c: Horizontal(g7)
    c: Coincident(g4,g-4)
    c: DistanceY(g4,g4) = 5.7
    c: DistanceY(g3,g3) = 5.7
    c: DistanceX(g2,g2) = 8
    c: DistanceX(g5,g5) = 8
FEATURE [PartDesign::Pad] Pad060
  BaseFeature = -> Pad059
  Direction = (0,0,-1)
  Length = 2.9
  Length2 = 10
  Profile = -> Sketch098
  ReferenceAxis = -> Sketch098 [N_Axis]
  Refine = true
  Reversed = true
  Suppressed = false
  Type = 0
FEATURE [PartDesign::Pad] Pad061
  BaseFeature = -> Pad060
  Direction = (0,0,-1)
  Length = 5
  Length2 = 10
  Profile = -> Pad060 [Face12]
  Refine = true
  Suppressed = false
  Type = 0
FEATURE [Sketcher::SketchObject] Sketch099
  ArcFitTolerance = 1e-06
  AttachmentSupport = -> [Pad061]
  ExternalGeometry = -> [Pad061]
  FullyConstrained = true
  MakeInternals = false
  MapMode = 5
  Placement = pos=(0,-8.8,0) rot=(1,0,0;1.5708rad)
  sketch-geometry (4):
    g0: LineSegment StartX=-34.8 StartY=-5 StartZ=0 EndX=-44.8 EndY=-4 EndZ=0
    g1: LineSegment StartX=-44.8 StartY=-4 StartZ=0 EndX=-44.8 EndY=2.9 EndZ=0
    g2: LineSegment StartX=-34.8 StartY=2.9 StartZ=0 EndX=-44.8 EndY=2.9 EndZ=0
    g3: LineSegment StartX=-34.8 StartY=2.9 StartZ=0 EndX=-34.8 EndY=-5 EndZ=0
  constraints (10):
    c: Coincident(g0,g-3)
    c: Coincident(g1,g0)
    c: Vertical(g1)
    c: Coincident(g2,g-3)
    c: Coincident(g2,g1)
    c: Horizontal(g2)
    c: DistanceX(g2,g2) = 10
    c: DistanceY(g1,g1) = 6.9
    c: Coincident(g3,g2)
    c: Coincident(g3,g0)
FEATURE [PartDesign::Pad] Pad062
  BaseFeature = -> Pad061
  Direction = (0,-1,2e-16)
  Length = 17.6
  Length2 = 10
  Profile = -> Sketch099
  ReferenceAxis = -> Sketch099 [N_Axis]
  Refine = true
  Reversed = true
  Suppressed = false
  Type = 0
FEATURE [Sketcher::SketchObject] Sketch100
  ArcFitTolerance = 1e-06
  AttachmentSupport = -> [Pad062]
  ExternalGeometry = -> [Pad062]
  FullyConstrained = true
  MakeInternals = false
  MapMode = 5
  Placement = pos=(0,0,-5) rot=(1,0,0;3.14159rad)
  sketch-geometry (4):
    g0: LineSegment StartX=-33.8 StartY=3.1 StartZ=0 EndX=-44.8 EndY=3.1 EndZ=0
    g1: LineSegment StartX=-44.8 StartY=3.1 StartZ=0 EndX=-44.8 EndY=-3.1 EndZ=0
    g2: LineSegment StartX=-44.8 StartY=-3.1 StartZ=0 EndX=-33.8 EndY=-3.1 EndZ=0
    g3: LineSegment StartX=-33.8 StartY=-3.1 StartZ=0 EndX=-33.8 EndY=3.1 EndZ=0
  constraints (10):
    c: Coincident(g0,g1)
    c: Coincident(g1,g2)
    c: Coincident(g2,g3)
    c: Coincident(g3,g0)
    c: Horizontal(g0)
    c: Horizontal(g2)
    c: Vertical(g1)
    c: Coincident(g0,g-3)
    c: PointOnObject(g1,g-5)
    c: Coincident(g2,g-4)
FEATURE [PartDesign::Pocket] Pocket049
  BaseFeature = -> Pad062
  Direction = (0,0,1)
  Length = 8
  Length2 = 5
  Profile = -> Sketch100
  ReferenceAxis = -> Sketch100 [N_Axis]
  Refine = true
  Suppressed = false
  Type = 0
FEATURE [Sketcher::SketchObject] Sketch101
  ArcFitTolerance = 1e-06
  AttachmentSupport = -> [Pocket049]
  ExternalGeometry = -> [Pocket049]
  FullyConstrained = true
  MakeInternals = false
  MapMode = 5
  Placement = pos=(0,0,-5) rot=(1,0,0;3.14159rad)
  sketch-geometry (8):
    g0: LineSegment StartX=-34.8 StartY=8.8 StartZ=0 EndX=-44.8 EndY=8.8 EndZ=0
    g1: LineSegment StartX=-44.8 StartY=8.8 StartZ=0 EndX=-44.8 EndY=8.3 EndZ=0
    g2: LineSegment StartX=-44.8 StartY=8.3 StartZ=0 EndX=-34.8 EndY=8.3 EndZ=0
    g3: LineSegment StartX=-34.8 StartY=8.3 StartZ=0 EndX=-34.8 EndY=8.8 EndZ=0
    g4: LineSegment StartX=-34.8 StartY=-8.8 StartZ=0 EndX=-34.8 EndY=-8.3 EndZ=0
    g5: LineSegment StartX=-34.8 StartY=-8.3 StartZ=0 EndX=-44.8 EndY=-8.3 EndZ=0
    g6: LineSegment StartX=-44.8 StartY=-8.3 StartZ=0 EndX=-44.8 EndY=-8.8 EndZ=0
    g7: LineSegment StartX=-44.8 StartY=-8.8 StartZ=0 EndX=-34.8 EndY=-8.8 EndZ=0
  constraints (22):
    c: Coincident(g0,g1)
    c: Coincident(g1,g2)
    c: Coincident(g2,g3)
    c: Coincident(g3,g0)
    c: Horizontal(g0)
    c: Horizontal(g2)
    c: Vertical(g1)
    c: Vertical(g3)
    c: Coincident(g0,g-4)
    c: PointOnObject(g1,g-7)
    c: DistanceY(g1,g1) = 0.5
    c: Coincident(g4,g5)
    c: Coincident(g5,g6)
    c: Coincident(g6,g7)
    c: Coincident(g7,g4)
    c: Vertical(g4)
    c: Vertical(g6)
    c: Horizontal(g5)
    c: Horizontal(g7)
    c: Coincident(g4,g-6)
    c: PointOnObject(g5,g-8)
    c: DistanceY(g6,g6) = 0.5
FEATURE [PartDesign::Pocket] Pocket050
  BaseFeature = -> Pocket049
  Direction = (0,0,1)
  Length = 8
  Length2 = 5
  Profile = -> Sketch101
  ReferenceAxis = -> Sketch101 [N_Axis]
  Refine = true
  Suppressed = false
  Type = 0
FEATURE [Sketcher::SketchObject] Sketch102
  ArcFitTolerance = 1e-06
  AttachmentSupport = -> [Pocket050]
  ExternalGeometry = -> [Pocket050]
  FullyConstrained = true
  MakeInternals = false
  MapMode = 5
  Placement = pos=(0,0,-5) rot=(1,0,0;3.14159rad)
  sketch-geometry (4):
    g0: LineSegment StartX=-33.8 StartY=3.1 StartZ=0 EndX=-33.8 EndY=-3.1 EndZ=0
    g1: LineSegment StartX=-33.8 StartY=-3.1 StartZ=0 EndX=-26.8 EndY=-3.1 EndZ=0
    g2: LineSegment StartX=-26.8 StartY=-3.1 StartZ=0 EndX=-26.8 EndY=3.1 EndZ=0
    g3: LineSegment StartX=-26.8 StartY=3.1 StartZ=0 EndX=-33.8 EndY=3.1 EndZ=0
  constraints (10):
    c: Coincident(g0,g1)
    c: Coincident(g1,g2)
    c: Coincident(g2,g3)
    c: Coincident(g3,g0)
    c: Vertical(g2)
    c: Horizontal(g1)
    c: Horizontal(g3)
    c: Coincident(g0,g-3)
    c: PointOnObject(g1,g-4)
    c: Coincident(g0,g-3)
FEATURE [PartDesign::Pocket] Pocket051
  BaseFeature = -> Pocket050
  Direction = (0,0,1)
  Length = 5
  Length2 = 5
  Profile = -> Sketch102
  ReferenceAxis = -> Sketch102 [N_Axis]
  Refine = true
  Suppressed = false
  Type = 0
FEATURE [Sketcher::SketchObject] Sketch103
  ArcFitTolerance = 1e-06
  AttachmentSupport = -> [Pocket051]
  ExternalGeometry = -> [Pocket051]
  FullyConstrained = true
  MakeInternals = false
  MapMode = 5
  Placement = pos=(0,8.8,0) rot=(0,0.707107,0.707107;3.14159rad)
  sketch-geometry (6):
    g0: LineSegment StartX=44.8 StartY=2.9 StartZ=0 EndX=64.8 EndY=2.9 EndZ=0
    g1: LineSegment StartX=64.8 StartY=2.9 StartZ=0 EndX=64.8 EndY=-4 EndZ=0
    g2: LineSegment StartX=44.8 StartY=2.9 StartZ=0 EndX=44.8 EndY=-5 EndZ=0
    g3: LineSegment StartX=44.8 StartY=-5 StartZ=0 EndX=55.3 EndY=-5 EndZ=0
    g4: LineSegment StartX=55.3 StartY=-5 StartZ=0 EndX=55.3 EndY=-4 EndZ=0
    g5: LineSegment StartX=55.3 StartY=-4 StartZ=0 EndX=64.8 EndY=-4 EndZ=0
  constraints (20):
    c: Coincident(g0,g-3)
    c: Horizontal(g0)
    c: Coincident(g1,g0)
    c: Vertical(g1)
    c: Coincident(g2,g0)
    c: Vertical(g2)
    c: Coincident(g3,g2)
    c: Horizontal(g3)
    c: Coincident(g4,g3)
    c: Vertical(g4)
    c: Coincident(g5,g4)
    c: Coincident(g5,g1)
    c: Horizontal(g5)
    c: DistanceX(g0,g0) = 20
    c: DistanceX(g-4,g0) = 38
    c: DistanceX(g3,g3) = 10.5
    c: DistanceY(g2,g2) = 7.9
    c: DistanceY(g1,g1) = 6.9
    c: DistanceY(g-4,g-4) = 7.9
    c: DistanceY(g-3,g0) = 6.9
FEATURE [PartDesign::Pad] Pad063
  BaseFeature = -> Pocket051
  Direction = (0,1,-2e-16)
  Length = 17.6
  Length2 = 10
  Profile = -> Sketch103
  ReferenceAxis = -> Sketch103 [N_Axis]
  Refine = true
  Reversed = true
  Suppressed = false
  Type = 0
FEATURE [Sketcher::SketchObject] Sketch104
  ArcFitTolerance = 1e-06
  AttachmentSupport = -> [Pad063]
  ExternalGeometry = -> [Pad063]
  FullyConstrained = true
  MakeInternals = false
  MapMode = 5
  Placement = pos=(0,-1.1e-15,-5) rot=(1,0,0;3.14159rad)
  sketch-geometry (8):
    g0: LineSegment StartX=-44.8 StartY=3.1 StartZ=0 EndX=-51.6 EndY=3.1 EndZ=0
    g1: LineSegment StartX=-51.6 StartY=3.1 StartZ=0 EndX=-51.6 EndY=4 EndZ=0
    g2: LineSegment StartX=-51.6 StartY=4 StartZ=0 EndX=-64.8 EndY=4 EndZ=0
    g3: LineSegment StartX=-44.8 StartY=-3.1 StartZ=0 EndX=-51.6 EndY=-3.1 EndZ=0
    g4: LineSegment StartX=-51.6 StartY=-3.1 StartZ=0 EndX=-51.6 EndY=-4 EndZ=0
    g5: LineSegment StartX=-51.6 StartY=-4 StartZ=0 EndX=-64.8 EndY=-4 EndZ=0
    g6: LineSegment StartX=-64.8 StartY=4 StartZ=0 EndX=-64.8 EndY=-4 EndZ=0
    g7: LineSegment StartX=-44.8 StartY=3.1 StartZ=0 EndX=-44.8 EndY=-3.1 EndZ=0
  constraints (22):
    c: Coincident(g0,g-5)
    c: Horizontal(g0)
    c: Coincident(g1,g0)
    c: Vertical(g1)
    c: Coincident(g2,g1)
    c: PointOnObject(g2,g-4)
    c: Horizontal(g2)
    c: Coincident(g3,g-6)
    c: Horizontal(g3)
    c: Coincident(g4,g3)
    c: Vertical(g4)
    c: Coincident(g5,g4)
    c: PointOnObject(g5,g-4)
    c: Horizontal(g5)
    c: DistanceX(g2,g2) = 13.2
    c: DistanceX(g5,g5) = 13.2
    c: DistanceY(g-4,g5) = 4.8
    c: DistanceY(g2,g-4) = 4.8
    c: Coincident(g6,g2)
    c: Coincident(g6,g5)
    c: Coincident(g7,g0)
    c: Coincident(g7,g3)
FEATURE [PartDesign::Pocket] Pocket052
  BaseFeature = -> Pad063
  Direction = (0,0,1)
  Length = 8
  Length2 = 5
  Profile = -> Sketch104
  ReferenceAxis = -> Sketch104 [N_Axis]
  Refine = true
  Suppressed = false
  Type = 0
FEATURE [Sketcher::SketchObject] Sketch105
  ArcFitTolerance = 1e-06
  AttachmentSupport = -> [Pocket052]
  ExternalGeometry = -> [Pocket052]
  FullyConstrained = true
  MakeInternals = false
  MapMode = 5
  Placement = pos=(0,8.8,-2.1e-15) rot=(0,0.707107,0.707107;3.14159rad)
  sketch-geometry (4):
    g0: LineSegment StartX=62.6 StartY=2.9 StartZ=0 EndX=62.6 EndY=0.1 EndZ=0
    g1: LineSegment StartX=60.6 StartY=2.9 StartZ=0 EndX=60.6 EndY=0.0999899 EndZ=0
    g2: ArcOfCircle CenterX=61.6 CenterY=0.1 CenterZ=0 NormalX=0 NormalY=0 NormalZ=1 AngleXU=0 Radius=1 StartAngle=3.1416 EndAngle=6.28319
    g3: LineSegment StartX=60.6 StartY=2.9 StartZ=0 EndX=62.6 EndY=2.9 EndZ=0
  constraints (13):
    c: PointOnObject(g0,g-3)
    c: Vertical(g0)
    c: PointOnObject(g1,g-3)
    c: Vertical(g1)
    c: Coincident(g2,g0)
    c: Coincident(g2,g1)
    c: Coincident(g3,g1)
    c: Coincident(g3,g0)
    c: DistanceX(g3,g3) = 2
    c: Diameter(g2) = 2
    c: DistanceY(g0,g2) = 0
    c: DistanceX(g0,g-4) = 2.2
    c: DistanceY(g-5,g0) = 4.1
FEATURE [PartDesign::Pocket] Pocket053
  BaseFeature = -> Pocket052
  Direction = (0,-1,2e-16)
  Length = 18
  Length2 = 5
  Profile = -> Sketch105
  ReferenceAxis = -> Sketch105 [N_Axis]
  Refine = true
  Suppressed = false
  Type = 0
FEATURE [Sketcher::SketchObject] Sketch106
  ArcFitTolerance = 1e-06
  AttachmentSupport = -> [Pocket053]
  ExternalGeometry = -> [Pocket053]
  FullyConstrained = true
  MakeInternals = false
  MapMode = 5
  Placement = pos=(0,-9e-16,-4) rot=(1,0,0;3.14159rad)
  sketch-geometry (8):
    g0: LineSegment StartX=-62.6 StartY=7.15 StartZ=0 EndX=-62.6 EndY=5.65 EndZ=0
    g1: LineSegment StartX=-62.6 StartY=5.65 StartZ=0 EndX=-60.6 EndY=5.65 EndZ=0
    g2: LineSegment StartX=-60.6 StartY=5.65 StartZ=0 EndX=-60.6 EndY=7.15 EndZ=0
    g3: LineSegment StartX=-60.6 StartY=7.15 StartZ=0 EndX=-62.6 EndY=7.15 EndZ=0
    g4: LineSegment StartX=-62.6 StartY=-5.65 StartZ=0 EndX=-62.6 EndY=-7.15 EndZ=0
    g5: LineSegment StartX=-62.6 StartY=-7.15 StartZ=0 EndX=-60.6 EndY=-7.15 EndZ=0
    g6: LineSegment StartX=-60.6 StartY=-7.15 StartZ=0 EndX=-60.6 EndY=-5.65 EndZ=0
    g7: LineSegment StartX=-60.6 StartY=-5.65 StartZ=0 EndX=-62.6 EndY=-5.65 EndZ=0
  constraints (26):
    c: Coincident(g0,g1)
    c: Coincident(g1,g2)
    c: Coincident(g2,g3)
    c: Coincident(g3,g0)
    c: Vertical(g0)
    c: Vertical(g2)
    c: Horizontal(g1)
    c: Horizontal(g3)
    c: Coincident(g4,g5)
    c: Coincident(g5,g6)
    c: Coincident(g6,g7)
    c: Coincident(g7,g4)
    c: Vertical(g4)
    c: Vertical(g6)
    c: Horizontal(g5)
    c: Horizontal(g7)
    c: DistanceX(g7,g7) = 2
    c: DistanceX(g3,g3) = 2
    c: DistanceY(g0,g0) = 1.5
    c: DistanceY(g4,g4) = 1.5
    c: DistanceX(g-8,g4) = 2.2
    c: DistanceX(g-5,g0) = 2.2
    c: DistanceY(g-4,g-4) = 4.8
    c: DistanceY(g-7,g-7) = 4.8
    c: DistanceY(g0,g-4) = 1.65
    c: DistanceY(g4,g-7) = 1.65
FEATURE [PartDesign::Pocket] Pocket054
  BaseFeature = -> Pocket053
  Direction = (0,0,1)
  Length = 5
  Length2 = 5
  Profile = -> Sketch106
  ReferenceAxis = -> Sketch106 [N_Axis]
  Refine = true
  Suppressed = false
  Type = 0
FEATURE [Sketcher::SketchObject] Sketch107
  ArcFitTolerance = 1e-06
  AttachmentSupport = -> [Pocket054]
  ExternalGeometry = -> [Pocket054]
  FullyConstrained = true
  MakeInternals = false
  MapMode = 5
  Placement = pos=(0,0,2.9) rot=(0,0,1;0rad)
  sketch-geometry (8):
    g0: LineSegment StartX=-62.6 StartY=7.15 StartZ=0 EndX=-62.6 EndY=5.65 EndZ=0
    g1: LineSegment StartX=-62.6 StartY=5.65 StartZ=0 EndX=-60.6 EndY=5.65 EndZ=0
    g2: LineSegment StartX=-60.6 StartY=5.65 StartZ=0 EndX=-60.6 EndY=7.15 EndZ=0
    g3: LineSegment StartX=-60.6 StartY=7.15 StartZ=0 EndX=-62.6 EndY=7.15 EndZ=0
    g4: LineSegment StartX=-62.6 StartY=-5.65 StartZ=0 EndX=-62.6 EndY=-7.15 EndZ=0
    g5: LineSegment StartX=-62.6 StartY=-7.15 StartZ=0 EndX=-60.6 EndY=-7.15 EndZ=0
    g6: LineSegment StartX=-60.6 StartY=-7.15 StartZ=0 EndX=-60.6 EndY=-5.65 EndZ=0
    g7: LineSegment StartX=-60.6 StartY=-5.65 StartZ=0 EndX=-62.6 EndY=-5.65 EndZ=0
  constraints (20):
    c: Coincident(g0,g1)
    c: Coincident(g1,g2)
    c: Coincident(g2,g3)
    c: Coincident(g3,g0)
    c: Vertical(g0)
    c: Vertical(g2)
    c: Horizontal(g1)
    c: Horizontal(g3)
    c: Coincident(g0,g-3)
    c: Coincident(g1,g-5)
    c: Coincident(g4,g5)
    c: Coincident(g5,g6)
    c: Coincident(g6,g7)
    c: Coincident(g7,g4)
    c: Vertical(g4)
    c: Vertical(g6)
    c: Horizontal(g5)
    c: Horizontal(g7)
    c: Coincident(g4,g-6)
    c: Coincident(g5,g-8)
FEATURE [PartDesign::Pad] Pad064
  BaseFeature = -> Pocket054
  Direction = (0,0,1)
  Length = 3
  Length2 = 10
  Profile = -> Sketch107
  ReferenceAxis = -> Sketch107 [N_Axis]
  Refine = true
  Reversed = true
  Suppressed = false
  Type = 0
FEATURE [Sketcher::SketchObject] Sketch108
  ArcFitTolerance = 1e-06
  AttachmentSupport = -> [Pad064]
  ExternalGeometry = -> [Pad064]
  FullyConstrained = true
  MakeInternals = false
  MapMode = 5
  Placement = pos=(0,-7.15,0) rot=(1,0,0;1.5708rad)
  sketch-geometry (5):
    g0: Circle CenterX=-61.6 CenterY=0.1 CenterZ=0 NormalX=0 NormalY=0 NormalZ=1 AngleXU=0 Radius=1
    g1: LineSegment StartX=-62.6 StartY=2.9 StartZ=0 EndX=-62.6 EndY=2.4 EndZ=0
    g2: LineSegment StartX=-62.6 StartY=2.4 StartZ=0 EndX=-60.6 EndY=2.4 EndZ=0
    g3: LineSegment StartX=-60.6 StartY=2.4 StartZ=0 EndX=-60.6 EndY=2.9 EndZ=0
    g4: LineSegment StartX=-60.6 StartY=2.9 StartZ=0 EndX=-62.6 EndY=2.9 EndZ=0
  constraints (13):
    c: Coincident(g0,g-3)
    c: Equal(g0,g-3)
    c: Coincident(g1,g2)
    c: Coincident(g2,g3)
    c: Coincident(g3,g4)
    c: Coincident(g4,g1)
    c: Vertical(g1)
    c: Vertical(g3)
    c: Horizontal(g2)
    c: Horizontal(g4)
    c: Coincident(g1,g-6)
    c: PointOnObject(g2,g-5)
    c: DistanceY(g3,g3) = 0.5
FEATURE [PartDesign::Pocket] Pocket055
  BaseFeature = -> Pad064
  Direction = (0,1,-2e-16)
  Length = 15
  Length2 = 5
  Profile = -> Sketch108
  ReferenceAxis = -> Sketch108 [N_Axis]
  Refine = true
  Suppressed = false
  Type = 0
FEATURE [Sketcher::SketchObject] Sketch109
  ArcFitTolerance = 1e-06
  AttachmentSupport = -> [Pocket055]
  ExternalGeometry = -> [Pocket055]
  FullyConstrained = true
  MakeInternals = false
  MapMode = 5
  Placement = pos=(0,-9e-16,-4) rot=(1,0,0;3.14159rad)
  sketch-geometry (6):
    g0: LineSegment StartX=-64.8 StartY=8.8 StartZ=0 EndX=-62.6 EndY=8.8 EndZ=0
    g1: LineSegment StartX=-62.6 StartY=8.8 StartZ=0 EndX=-64.8 EndY=6.6 EndZ=0
    g2: LineSegment StartX=-64.8 StartY=6.6 StartZ=0 EndX=-64.8 EndY=8.8 EndZ=0
    g3: LineSegment StartX=-64.8 StartY=-8.8 StartZ=0 EndX=-64.8 EndY=-6.6 EndZ=0
    g4: LineSegment StartX=-64.8 StartY=-6.6 StartZ=0 EndX=-62.6 EndY=-8.8 EndZ=0
    g5: LineSegment StartX=-62.6 StartY=-8.8 StartZ=0 EndX=-64.8 EndY=-8.8 EndZ=0
  constraints (16):
    c: Coincident(g0,g-4)
    c: PointOnObject(g0,g-3)
    c: Coincident(g1,g0)
    c: PointOnObject(g1,g-4)
    c: Coincident(g2,g1)
    c: Coincident(g2,g0)
    c: DistanceX(g0,g0) = 2.2
    c: DistanceY(g2,g2) = 2.2
    c: Coincident(g3,g-6)
    c: PointOnObject(g3,g-6)
    c: Coincident(g4,g3)
    c: Coincident(g5,g4)
    c: Coincident(g5,g3)
    c: PointOnObject(g4,g-7)
    c: DistanceX(g5,g5) = 2.2
    c: DistanceY(g3,g3) = 2.2
FEATURE [PartDesign::Pocket] Pocket056
  BaseFeature = -> Pocket055
  Direction = (0,0,1)
  Length = 1.5
  Length2 = 5
  Profile = -> Sketch109
  ReferenceAxis = -> Sketch109 [N_Axis]
  Refine = true
  Suppressed = false
  Type = 0
FEATURE [Sketcher::SketchObject] Sketch110
  ArcFitTolerance = 1e-06
  AttachmentSupport = -> [Pocket056]
  ExternalGeometry = -> [Pocket056]
  FullyConstrained = true
  MakeInternals = false
  MapMode = 5
  Placement = pos=(0,1.1e-15,2.9) rot=(0,0,1;0rad)
  sketch-geometry (20):
    g0: LineSegment StartX=-28.3 StartY=7.3 StartZ=0 EndX=-28.3 EndY=4.6 EndZ=0
    g1: LineSegment StartX=-28.3 StartY=4.6 StartZ=0 EndX=-50.1 EndY=4.6 EndZ=0
    g2: LineSegment StartX=-51 StartY=5.5 StartZ=0 EndX=-60.1 EndY=5.5 EndZ=0
    g3: LineSegment StartX=-60.1 StartY=5.5 StartZ=0 EndX=-60.1 EndY=7.3 EndZ=0
    g4: LineSegment StartX=-60.1 StartY=7.3 StartZ=0 EndX=-46.3 EndY=7.3 EndZ=0
    g5: LineSegment StartX=-45.8 StartY=6.8 StartZ=0 EndX=-33.8 EndY=6.8 EndZ=0
    g6: LineSegment StartX=-33.3 StartY=7.3 StartZ=0 EndX=-28.3 EndY=7.3 EndZ=0
    g7: ArcOfCircle CenterX=-51 CenterY=4.6 CenterZ=0 NormalX=0 NormalY=0 NormalZ=1 AngleXU=0 Radius=0.9 StartAngle=0 EndAngle=1.5708
    g8: ArcOfCircle CenterX=-45.8 CenterY=7.3 CenterZ=0 NormalX=0 NormalY=0 NormalZ=1 AngleXU=0 Radius=0.5 StartAngle=3.14159 EndAngle=4.71239
    g9: ArcOfCircle CenterX=-33.8 CenterY=7.3 CenterZ=0 NormalX=0 NormalY=0 NormalZ=1 AngleXU=0 Radius=0.5 StartAngle=4.71239 EndAngle=6.28319
    g10: LineSegment StartX=-60.1 StartY=-5.5 StartZ=0 EndX=-60.1 EndY=-7.3 EndZ=0
    g11: LineSegment StartX=-60.1 StartY=-7.3 StartZ=0 EndX=-46.3 EndY=-7.3 EndZ=0
    g12: LineSegment StartX=-33.3 StartY=-7.3 StartZ=0 EndX=-28.3 EndY=-7.3 EndZ=0
    g13: LineSegment StartX=-28.3 StartY=-7.3 StartZ=0 EndX=-28.3 EndY=-4.6 EndZ=0
    g14: LineSegment StartX=-28.3 StartY=-4.6 StartZ=0 EndX=-50.1 EndY=-4.6 EndZ=0
    g15: LineSegment StartX=-51 StartY=-5.5 StartZ=0 EndX=-60.1 EndY=-5.5 EndZ=0
    g16: ArcOfCircle CenterX=-51 CenterY=-4.6 CenterZ=0 NormalX=0 NormalY=0 NormalZ=1 AngleXU=0 Radius=0.9 StartAngle=4.71239 EndAngle=6.28319
    g17: ArcOfCircle CenterX=-45.8 CenterY=-7.3 CenterZ=0 NormalX=0 NormalY=0 NormalZ=1 AngleXU=0 Radius=0.5 StartAngle=1.5708 EndAngle=3.14159
    g18: ArcOfCircle CenterX=-33.8 CenterY=-7.3 CenterZ=0 NormalX=0 NormalY=0 NormalZ=1 AngleXU=0 Radius=0.5 StartAngle=4e-16 EndAngle=1.5708
    g19: LineSegment StartX=-45.8 StartY=-6.8 StartZ=0 EndX=-33.8 EndY=-6.8 EndZ=0
  constraints (67):
    c: Vertical(g10)
    c: Coincident(g13,g12)
    c: Horizontal(g12)
    c: Horizontal(g14)
    c: Horizontal(g15)
    c: Horizontal(g11)
    c: DistanceX(g13,g-12) = 1.5
    c: Vertical(g13)
    c: DistanceY(g13,g-12) = 1.5
    c: DistanceY(g-13,g12) = 1.5
    c: DistanceY(g-14,g18) = 1.5
    c: DistanceY(g18,g12) = 0
    c: DistanceX(g18,g18) = 0
    c: Coincident(g18,g12)
    c: Coincident(g17,g11)
    c: Radius(g17) = 0.5
    c: Coincident(g19,g17)
    c: Coincident(g19,g18)
    c: Horizontal(g19)
    c: Coincident(g16,g14)
    c: Coincident(g14,g13)
    c: Coincident(g15,g16)
    c: Coincident(g10,g15)
    c: Coincident(g10,g11)
    c: DistanceX(g-13,g12) = 1.5
    c: DistanceX(g-11,g14) = 1.5
    c: DistanceX(g16,g15) = 0
    c: DistanceX(g17,g17) = 0
    c: DistanceY(g16,g14) = 0
    c: DistanceY(g11,g17) = 0
    c: DistanceX(g11,g-15) = 1.5
    c: DistanceX(g-16,g10) = 0.5
    c: Coincident(g7,g1)
    c: Coincident(g0,g6)
    c: Coincident(g0,g1)
    c: Coincident(g6,g9)
    c: Coincident(g5,g9)
    c: Coincident(g5,g8)
    c: Coincident(g8,g4)
    c: Coincident(g3,g4)
    c: Coincident(g3,g2)
    c: DistanceX(g0,g-7) = 1.5
    c: Vertical(g0)
    c: Vertical(g3)
    c: Horizontal(g4)
    c: Horizontal(g2)
    c: Horizontal(g1)
    c: Horizontal(g5)
    c: Horizontal(g6)
    c: DistanceX(g9,g5) = 0
    c: DistanceX(g8,g5) = 0
    c: DistanceX(g2,g7) = 0
    c: DistanceY(g1,g7) = 0
    c: DistanceY(g8,g4) = 0
    c: DistanceY(g9,g6) = 0
    c: DistanceY(g-9,g2) = 1.5
    c: DistanceY(g4,g-10) = 1.5
    c: DistanceX(g-10,g3) = 0.5
    c: DistanceX(g-8,g1) = 1.5
    c: DistanceX(g4,g-10) = 1.5
    c: DistanceX(g-8,g-8) = 24.8
    c: Coincident(g2,g7)
    c: DistanceY(g0,g-7) = 1.5
    c: DistanceY(g5,g-5) = 1.5
    c: DistanceX(g-6,g6) = 1.5
    c: DistanceY(g-8,g0) = 1.5
    c: DistanceY(g15,g-16) = 1.5
FEATURE [PartDesign::Pocket] Pocket057
  BaseFeature = -> Pocket056
  Direction = (0,0,-1)
  Length = 3
  Length2 = 5
  Profile = -> Sketch110
  ReferenceAxis = -> Sketch110 [N_Axis]
  Refine = true
  Suppressed = false
  Type = 0
FEATURE [Sketcher::SketchObject] Sketch250
  ArcFitTolerance = 1e-06
  AttachmentSupport = -> [Pocket057]
  ExternalGeometry = -> [Pocket057]
  FullyConstrained = true
  MakeInternals = false
  MapMode = 5
  Placement = pos=(0,0,-5) rot=(1,0,0;3.14159rad)
  sketch-geometry (8):
    g0: LineSegment StartX=-26.8 StartY=8.8 StartZ=0 EndX=-26.8 EndY=3.1 EndZ=0
    g1: LineSegment StartX=-26.8 StartY=3.1 StartZ=0 EndX=-25.7 EndY=3.1 EndZ=0
    g2: LineSegment StartX=-25.7 StartY=3.1 StartZ=0 EndX=-25.7 EndY=8.8 EndZ=0
    g3: LineSegment StartX=-25.7 StartY=8.8 StartZ=0 EndX=-26.8 EndY=8.8 EndZ=0
    g4: LineSegment StartX=-26.8 StartY=-3.1 StartZ=0 EndX=-26.8 EndY=-8.8 EndZ=0
    g5: LineSegment StartX=-26.8 StartY=-8.8 StartZ=0 EndX=-25.7 EndY=-8.8 EndZ=0
    g6: LineSegment StartX=-25.7 StartY=-8.8 StartZ=0 EndX=-25.7 EndY=-3.1 EndZ=0
    g7: LineSegment StartX=-25.7 StartY=-3.1 StartZ=0 EndX=-26.8 EndY=-3.1 EndZ=0
  constraints (20):
    c: Coincident(g0,g1)
    c: Coincident(g1,g2)
    c: Coincident(g2,g3)
    c: Coincident(g3,g0)
    c: Vertical(g2)
    c: Horizontal(g1)
    c: Horizontal(g3)
    c: Coincident(g0,g-3)
    c: Coincident(g4,g5)
    c: Coincident(g5,g6)
    c: Coincident(g6,g7)
    c: Coincident(g7,g4)
    c: Vertical(g6)
    c: Horizontal(g5)
    c: Horizontal(g7)
    c: Coincident(g4,g-4)
    c: DistanceX(g7,g7) = 1.1
    c: Coincident(g4,g-4)
    c: Coincident(g0,g-3)
    c: DistanceX(g3,g3) = 1.1
FEATURE [PartDesign::Pad] Pad151
  BaseFeature = -> Pocket057
  Direction = (0,0,-1)
  Length = 7.9
  Length2 = 10
  Profile = -> Sketch250
  ReferenceAxis = -> Sketch250 [N_Axis]
  Refine = true
  Reversed = true
  Suppressed = false
  Type = 0
FEATURE [PartDesign::Fillet] Fillet008
  Base = -> Pad151 [Edge243,Edge220,Edge222,Edge166,Edge244,Edge195,Edge164,Edge156,Edge221,Edge96,Edge119,Edge98,Edge97,Edge120,Edge3,Edge21,Edge20,Edge157,Edge168,Edge155,Edge154,Edge9,Edge10,Edge5,Edge6,Edge14,Edge142,Edge144,Edge125,Edge167,Edge127,Edge152,Edge170,Edge171,Edge128,Edge149,Edge11,Edge12,Edge13,Edge34,+11 more]
  BaseFeature = -> Pad151
  Radius = 0.49
  Refine = true
  SupportTransform = false
  Suppressed = false
  UseAllEdges = false
FEATURE [PartDesign::Body] Body003  label="Legs"
  AllowCompound = false
  Group = -> [Binder001,Sketch097,Pad059,Sketch098,Pad060,Pad061,Sketch099,Pad062,Sketch100,Pocket049,Sketch101,Pocket050,Sketch102,Pocket051,Sketch103,Pad063,Sketch104,Pocket052,Sketch105,Pocket053,Sketch106,Pocket054,Sketch107,Pad064,Sketch108,Pocket055,Sketch109,Pocket056,Sketch110,Pocket057,Sketch250,Pad151,Fillet008]
  Origin = -> Origin003
  Tip = -> Fillet008
